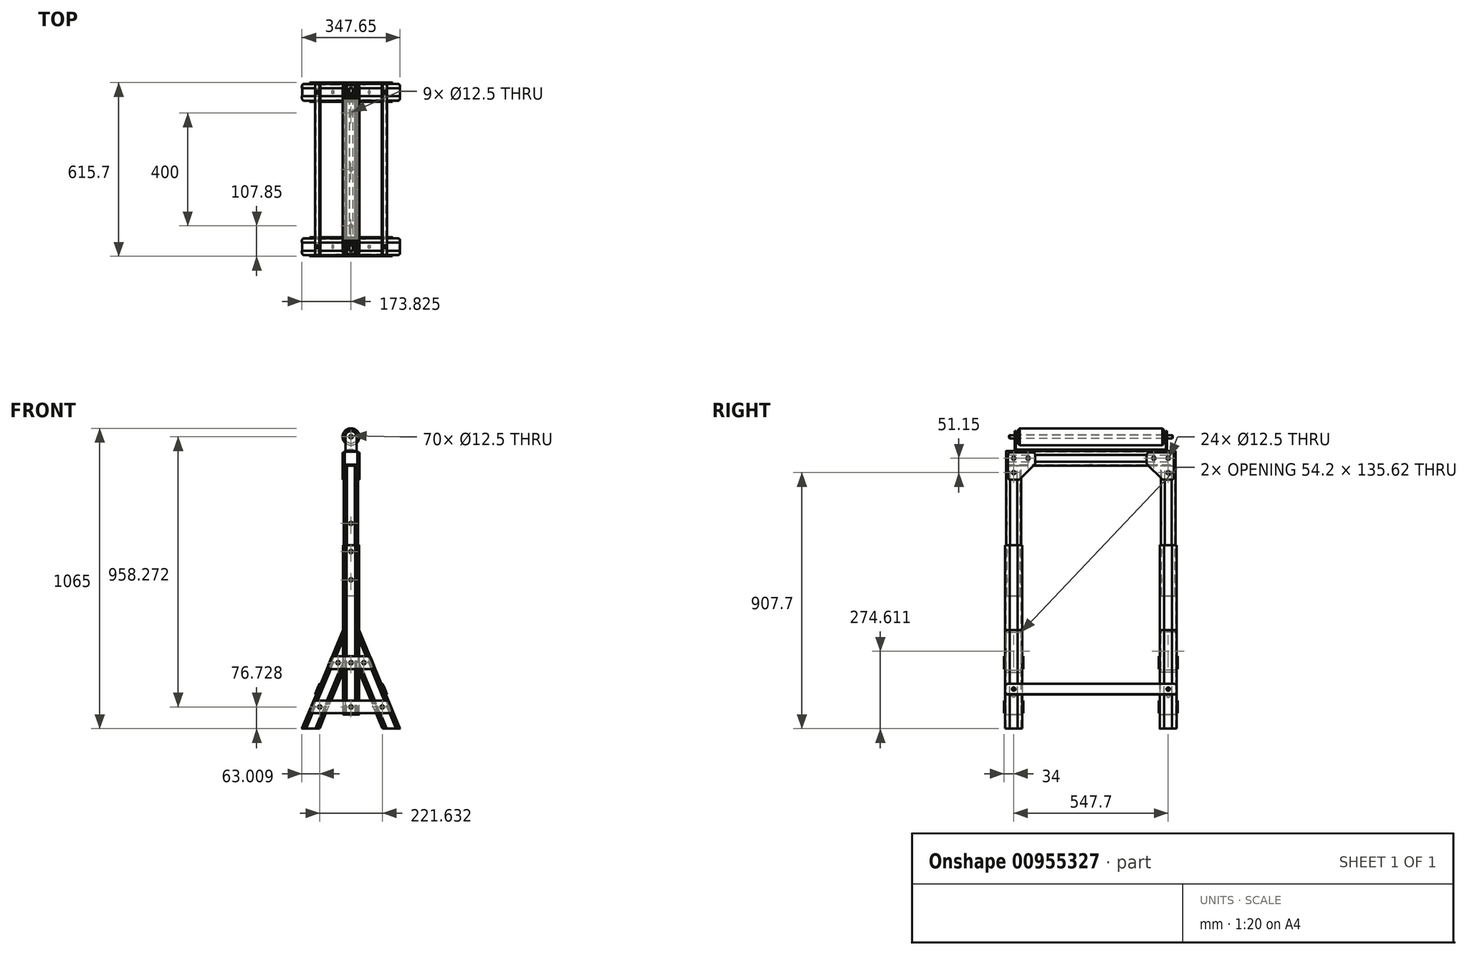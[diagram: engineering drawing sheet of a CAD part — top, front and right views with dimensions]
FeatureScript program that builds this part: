
annotation { "Feature Type Name" : "Feature", "Feature Type Description" : "" }
export const myFeature = defineFeature(function(context is Context, id is Id, definition is map)
    precondition{}
    {
        {
            var Q0;
            Q0=qCreatedBy(makeId("Front.planeOp"),FACE);
            var sketch = newSketch(context, id + "F0", { "sketchPlane" : qUnion([Q0])});
            skLineSegment(sketch, "E0", {"start": v(-144.97, 350) * mm, "end": v(0, 0) * mm});
            skLineSegment(sketch, "E1", {"start": v(0, 0) * mm, "end": v(-62.45, 0) * mm});
            skLineSegment(sketch, "E2", {"start": v(-62.45, 0) * mm, "end": v(-198.28, 327.92) * mm});
            skLineSegment(sketch, "E3", {"start": v(-198.28, 327.92) * mm, "end": v(-144.97, 350) * mm});
            skSolve(sketch);
        }
        {
            var Q0;
            Q0=makeQuery(id+"F0.imprint","IMPRINT",FACE,{"disambiguationData":[TD([[makeQuery(id+"F0.imprint","IMPRINT",EDGE,{"derivedFrom":sQuery(id+"F0.wireOp",EDGE,"E0")}),-1.0]])]});
            extrude(context, id + "F1", {"entities" : qUnion([Q0]), "depth" : 60 * mm, "offsetDistance" : 25 * mm});
        }
        {
            var Q0;
            Q0=makeQuery(id+"F1.opExtrude","CAP_EDGE",EDGE,{"disambiguationData":[OSD([sQuery(id+"F0.wireOp",EDGE,"E0")])],"isStart":false});
            var Q1;
            Q1=makeQuery(id+"F1.opExtrude","CAP_EDGE",EDGE,{"disambiguationData":[OSD([sQuery(id+"F0.wireOp",EDGE,"E0")])],"isStart":true});
            var Q2;
            Q2=makeQuery(id+"F1.opExtrude","CAP_EDGE",EDGE,{"disambiguationData":[OSD([sQuery(id+"F0.wireOp",EDGE,"E2")])],"isStart":true});
            var Q3;
            Q3=makeQuery(id+"F1.opExtrude","CAP_EDGE",EDGE,{"disambiguationData":[OSD([sQuery(id+"F0.wireOp",EDGE,"E2")])],"isStart":false});
            fillet(context, id + "F2", {"entities" : qUnion([Q0, Q1, Q2, Q3]), "radius" : 7.5 * mm, "tangentPropagation" : true, "allowEdgeOverflow" : false});
        }
        {
            var Q0;
            Q0=makeQuery(id+"F1.opExtrude","SWEPT_FACE",FACE,{"disambiguationData":[OSD([sQuery(id+"F0.wireOp",EDGE,"E3")])]});
            var sketch = newSketch(context, id + "F3", { "sketchPlane" : qUnion([Q0])});
            skArc(sketch, "E4.0", {"start": v(-50.2, -2.9) * mm, "mid": v(-53.45, -4.25) * mm, "end": v(-54.8, -7.5) * mm});
            skLineSegment(sketch, "E4.1", {"start": v(-54.8, -52.5) * mm, "end": v(-54.8, -7.5) * mm});
            skLineSegment(sketch, "E4.2", {"start": v(-50.2, -2.9) * mm, "end": v(-7.5, -2.9) * mm});
            skArc(sketch, "E4.3", {"start": v(-54.8, -52.5) * mm, "mid": v(-53.45, -55.75) * mm, "end": v(-50.2, -57.1) * mm});
            skArc(sketch, "E4.4", {"start": v(-2.9, -7.5) * mm, "mid": v(-4.25, -4.25) * mm, "end": v(-7.5, -2.9) * mm});
            skLineSegment(sketch, "E4.5", {"start": v(-2.9, -52.5) * mm, "end": v(-2.9, -7.5) * mm});
            skArc(sketch, "E4.6", {"start": v(-7.5, -57.1) * mm, "mid": v(-4.25, -55.75) * mm, "end": v(-2.9, -52.5) * mm});
            skLineSegment(sketch, "E4.7", {"start": v(-50.2, -57.1) * mm, "end": v(-7.5, -57.1) * mm});
            skLineSegment(sketch, "E5", {"start": v(-2.9, -7.5) * mm, "end": v(0, -7.5) * mm, "construction": true});
            skLineSegment(sketch, "E6", {"start": v(-2.9, -30) * mm, "end": v(0, -30) * mm, "construction": true});
            skLineSegment(sketch, "E7.0", {"start": v(-0.3, -44) * mm, "end": v(-0.3, -16) * mm});
            skLineSegment(sketch, "E8", {"start": v(-0.3, -16) * mm, "end": v(0, -16) * mm});
            skLineSegment(sketch, "E9", {"start": v(-0.3, -44) * mm, "end": v(0, -44) * mm});
            skLineSegment(sketch, "E10", {"start": v(-7.5, -57.1) * mm, "end": v(-7.5, -60) * mm, "construction": true});
            skLineSegment(sketch, "E11", {"start": v(-7.5, -60) * mm, "end": v(-8.5, -59) * mm});
            skLineSegment(sketch, "E12", {"start": v(-8.5, -59) * mm, "end": v(-9.5, -60) * mm});
            skLineSegment(sketch, "E13.1.0.0", {"start": v(-9.5, -60) * mm, "end": v(-10.5, -59) * mm});
            skLineSegment(sketch, "E13.1.0.1", {"start": v(-10.5, -59) * mm, "end": v(-11.5, -60) * mm});
            skLineSegment(sketch, "E13.2.0.0", {"start": v(-11.5, -60) * mm, "end": v(-12.5, -59) * mm});
            skLineSegment(sketch, "E13.2.0.1", {"start": v(-12.5, -59) * mm, "end": v(-13.5, -60) * mm});
            skLineSegment(sketch, "E13.direction1", {"start": v(-7.5, -60) * mm, "end": v(-9.5, -60) * mm, "construction": true});
            skLineSegment(sketch, "E14", {"start": v(-28.85, -60) * mm, "end": v(-28.85, -57.1) * mm, "construction": true});
            skLineSegment(sketch, "E15.MirrorCS", {"start": v(-50.2, -60) * mm, "end": v(-49.2, -59) * mm});
            skLineSegment(sketch, "E16.MirrorCS", {"start": v(-49.2, -59) * mm, "end": v(-48.2, -60) * mm});
            skLineSegment(sketch, "E17.MirrorCS", {"start": v(-48.2, -60) * mm, "end": v(-47.2, -59) * mm});
            skLineSegment(sketch, "E18.MirrorCS", {"start": v(-47.2, -59) * mm, "end": v(-46.2, -60) * mm});
            skLineSegment(sketch, "E19.MirrorCS", {"start": v(-46.2, -60) * mm, "end": v(-45.2, -59) * mm});
            skLineSegment(sketch, "E20.MirrorCS", {"start": v(-45.2, -59) * mm, "end": v(-44.2, -60) * mm});
            skLineSegment(sketch, "E21.MirrorCS", {"start": v(-57.4, -16) * mm, "end": v(-57.7, -16) * mm});
            skLineSegment(sketch, "E22.MirrorCS", {"start": v(-57.4, -44) * mm, "end": v(-57.4, -16) * mm});
            skLineSegment(sketch, "E23.MirrorCS", {"start": v(-57.4, -44) * mm, "end": v(-57.7, -44) * mm});
            skLineSegment(sketch, "E24.MirrorCS", {"start": v(-7.5, 0) * mm, "end": v(-8.5, -1) * mm});
            skLineSegment(sketch, "E25.MirrorCS", {"start": v(-8.5, -1) * mm, "end": v(-9.5, 0) * mm});
            skLineSegment(sketch, "E26.MirrorCS", {"start": v(-9.5, 0) * mm, "end": v(-10.5, -1) * mm});
            skLineSegment(sketch, "E27.MirrorCS", {"start": v(-10.5, -1) * mm, "end": v(-11.5, 0) * mm});
            skLineSegment(sketch, "E28.MirrorCS", {"start": v(-11.5, 0) * mm, "end": v(-12.5, -1) * mm});
            skLineSegment(sketch, "E29.MirrorCS", {"start": v(-12.5, -1) * mm, "end": v(-13.5, 0) * mm});
            skLineSegment(sketch, "E30.MirrorCS", {"start": v(-45.2, -1) * mm, "end": v(-44.2, 0) * mm});
            skLineSegment(sketch, "E31.MirrorCS", {"start": v(-46.2, 0) * mm, "end": v(-45.2, -1) * mm});
            skLineSegment(sketch, "E32.MirrorCS", {"start": v(-47.2, -1) * mm, "end": v(-46.2, 0) * mm});
            skLineSegment(sketch, "E33.MirrorCS", {"start": v(-48.2, 0) * mm, "end": v(-47.2, -1) * mm});
            skLineSegment(sketch, "E34.MirrorCS", {"start": v(-49.2, -1) * mm, "end": v(-48.2, 0) * mm});
            skLineSegment(sketch, "E35.MirrorCS", {"start": v(-50.2, 0) * mm, "end": v(-49.2, -1) * mm});
            skSolve(sketch);
        }
        {
            var Q0;
            {var subQ0=sQuery(id+"F3.wireOp",EDGE,"E24.MirrorCS");Q0=makeQuery(id+"F3.imprint","IMPRINT",FACE,{"disambiguationData":[TD([[makeQuery(id+"F3.imprint","IMPRINT",EDGE,{"derivedFrom":subQ0}),-1.0]])]});}
            var Q1;
            {var subQ0=sQuery(id+"F3.wireOp",EDGE,"E26.MirrorCS");Q1=makeQuery(id+"F3.imprint","IMPRINT",FACE,{"disambiguationData":[TD([[makeQuery(id+"F3.imprint","IMPRINT",EDGE,{"derivedFrom":subQ0}),-1.0]])]});}
            var Q2;
            {var subQ0=sQuery(id+"F3.wireOp",EDGE,"E28.MirrorCS");Q2=makeQuery(id+"F3.imprint","IMPRINT",FACE,{"disambiguationData":[TD([[makeQuery(id+"F3.imprint","IMPRINT",EDGE,{"derivedFrom":subQ0}),-1.0]])]});}
            var Q3;
            Q3=makeQuery(id+"F3.imprint","IMPRINT",FACE,{"disambiguationData":[TD([[makeQuery(id+"F3.imprint","IMPRINT",EDGE,{"derivedFrom":sQuery(id+"F3.wireOp",EDGE,"E4.0")}),1.0]])]});
            var Q4;
            {var subQ0=sQuery(id+"F3.wireOp",EDGE,"E30.MirrorCS");Q4=makeQuery(id+"F3.imprint","IMPRINT",FACE,{"disambiguationData":[TD([[makeQuery(id+"F3.imprint","IMPRINT",EDGE,{"derivedFrom":subQ0}),1.0]])]});}
            var Q5;
            {var subQ0=sQuery(id+"F3.wireOp",EDGE,"E32.MirrorCS");Q5=makeQuery(id+"F3.imprint","IMPRINT",FACE,{"disambiguationData":[TD([[makeQuery(id+"F3.imprint","IMPRINT",EDGE,{"derivedFrom":subQ0}),1.0]])]});}
            var Q6;
            {var subQ0=sQuery(id+"F3.wireOp",EDGE,"E34.MirrorCS");Q6=makeQuery(id+"F3.imprint","IMPRINT",FACE,{"disambiguationData":[TD([[makeQuery(id+"F3.imprint","IMPRINT",EDGE,{"derivedFrom":subQ0}),1.0]])]});}
            var Q7;
            {var subQ0=sQuery(id+"F3.wireOp",EDGE,"E21.MirrorCS");Q7=makeQuery(id+"F3.imprint","IMPRINT",FACE,{"disambiguationData":[TD([[makeQuery(id+"F3.imprint","IMPRINT",EDGE,{"derivedFrom":subQ0}),1.0]])]});}
            var Q8;
            {var subQ0=sQuery(id+"F3.wireOp",EDGE,"E15.MirrorCS");Q8=makeQuery(id+"F3.imprint","IMPRINT",FACE,{"disambiguationData":[TD([[makeQuery(id+"F3.imprint","IMPRINT",EDGE,{"derivedFrom":subQ0}),-1.0]])]});}
            var Q9;
            {var subQ0=sQuery(id+"F3.wireOp",EDGE,"E17.MirrorCS");Q9=makeQuery(id+"F3.imprint","IMPRINT",FACE,{"disambiguationData":[TD([[makeQuery(id+"F3.imprint","IMPRINT",EDGE,{"derivedFrom":subQ0}),-1.0]])]});}
            var Q10;
            {var subQ0=sQuery(id+"F3.wireOp",EDGE,"E19.MirrorCS");Q10=makeQuery(id+"F3.imprint","IMPRINT",FACE,{"disambiguationData":[TD([[makeQuery(id+"F3.imprint","IMPRINT",EDGE,{"derivedFrom":subQ0}),-1.0]])]});}
            var Q11;
            {var subQ0=sQuery(id+"F3.wireOp",EDGE,"E11");Q11=makeQuery(id+"F3.imprint","IMPRINT",FACE,{"disambiguationData":[TD([[makeQuery(id+"F3.imprint","IMPRINT",EDGE,{"derivedFrom":subQ0}),1.0]])]});}
            var Q12;
            {var subQ0=sQuery(id+"F3.wireOp",EDGE,"E13.1.0.0");Q12=makeQuery(id+"F3.imprint","IMPRINT",FACE,{"disambiguationData":[TD([[makeQuery(id+"F3.imprint","IMPRINT",EDGE,{"derivedFrom":subQ0}),1.0]])]});}
            var Q13;
            {var subQ0=sQuery(id+"F3.wireOp",EDGE,"E13.2.0.0");Q13=makeQuery(id+"F3.imprint","IMPRINT",FACE,{"disambiguationData":[TD([[makeQuery(id+"F3.imprint","IMPRINT",EDGE,{"derivedFrom":subQ0}),1.0]])]});}
            var Q14;
            Q14=makeQuery(id+"F3.imprint","IMPRINT",FACE,{"disambiguationData":[TD([[makeQuery(id+"F3.imprint","IMPRINT",EDGE,{"derivedFrom":sQuery(id+"F3.wireOp",EDGE,"E7.0")}),-1.0]])]});
            extrude(context, id + "F4", {"entities" : qUnion([Q0, Q1, Q2, Q3, Q4, Q5, Q6, Q7, Q8, Q9, Q10, Q11, Q12, Q13, Q14]), "operationType" : NewBodyOperationType.REMOVE, "endBound" : BoundingType.THROUGH_ALL, "oppositeDirection" : true, "depth" : 25 * mm, "offsetDistance" : 25 * mm});
        }
        {
            var Q0;
            Q0=makeQuery(id+"F4.boolean.opBoolean","COPY",FACE,{"derivedFrom":makeQuery(id+"F4.opExtrude","SWEPT_FACE",FACE,{"disambiguationData":[OSD([sQuery(id+"F3.wireOp",EDGE,"E7.0")])]})});
            var sketch = newSketch(context, id + "F5", { "sketchPlane" : qUnion([Q0])});
            skCircle(sketch, "E36", {"center": v(-30, 150.12) * mm, "radius": 6.25 * mm});
            skSolve(sketch);
        }
        {
            var Q0;
            Q0 = qSketchRegion(id + "F5", true);
            var Q1;
            Q1=makeQuery(id+"F4.boolean.opBoolean","COPY",FACE,{"derivedFrom":makeQuery(id+"F4.opExtrude","SWEPT_FACE",FACE,{"disambiguationData":[OSD([sQuery(id+"F3.wireOp",EDGE,"E22.MirrorCS")])]})});
            extrude(context, id + "F6", {"entities" : qUnion([Q0]), "operationType" : NewBodyOperationType.REMOVE, "endBound" : BoundingType.UP_TO_SURFACE, "oppositeDirection" : true, "depth" : 25 * mm, "endBoundEntityFace" : qUnion([Q1]), "offsetDistance" : 25 * mm});
        }
        {
            var Q0;
            Q0=makeQuery(id+"F1.opExtrude","CAP_FACE",FACE,{"disambiguationData":[OSD([sQuery(id+"F0.wireOp",EDGE,"E0"),sQuery(id+"F0.wireOp",EDGE,"E1"),sQuery(id+"F0.wireOp",EDGE,"E2"),sQuery(id+"F0.wireOp",EDGE,"E3")])],"isStart":false});
            var sketch = newSketch(context, id + "F7", { "sketchPlane" : qUnion([Q0])});
            skLineSegment(sketch, "E37", {"start": v(-198.28, 327.92) * mm, "end": v(-144.97, 350) * mm});
            skLineSegment(sketch, "E38", {"start": v(-144.97, 350) * mm, "end": v(-144.97, 199.22) * mm});
            skLineSegment(sketch, "E39", {"start": v(-144.97, 199.22) * mm, "end": v(-198.28, 327.92) * mm});
            skSolve(sketch);
        }
        {
            var Q0;
            Q0=qSketchRegion(id+"F7",true);
            var Q1;
            Q1=makeQuery(id+"F1.opExtrude","CAP_FACE",FACE,{"disambiguationData":[OSD([sQuery(id+"F0.wireOp",EDGE,"E0"),sQuery(id+"F0.wireOp",EDGE,"E1"),sQuery(id+"F0.wireOp",EDGE,"E2"),sQuery(id+"F0.wireOp",EDGE,"E3")])],"isStart":true});
            extrude(context, id + "F8", {"entities" : qUnion([Q0]), "operationType" : NewBodyOperationType.REMOVE, "endBound" : BoundingType.UP_TO_SURFACE, "oppositeDirection" : true, "depth" : 25 * mm, "endBoundEntityFace" : qUnion([Q1]), "offsetDistance" : 25 * mm});
        }
        {
            var Q0;
            Q0=makeQuery(id+"F1.opExtrude","CAP_FACE",FACE,{"disambiguationData":[OSD([sQuery(id+"F0.wireOp",EDGE,"E0"),sQuery(id+"F0.wireOp",EDGE,"E1"),sQuery(id+"F0.wireOp",EDGE,"E2"),sQuery(id+"F0.wireOp",EDGE,"E3")])],"isStart":false});
            var sketch = newSketch(context, id + "F9", { "sketchPlane" : qUnion([Q0])});
            skLineSegment(sketch, "E40", {"start": v(-202.67, 650) * mm, "end": v(-202.67, 50) * mm});
            skLineSegment(sketch, "E41", {"start": v(-202.67, 50) * mm, "end": v(-144.97, 50) * mm});
            skLineSegment(sketch, "E42", {"start": v(-144.97, 50) * mm, "end": v(-144.97, 650) * mm});
            skLineSegment(sketch, "E43", {"start": v(-144.97, 650) * mm, "end": v(-202.67, 650) * mm});
            skSolve(sketch);
        }
        {
            var Q0;
            Q0 = qSketchRegion(id + "F9", true);
            extrude(context, id + "F10", {"entities" : qUnion([Q0]), "oppositeDirection" : true, "depth" : 60 * mm, "offsetDistance" : 25 * mm});
        }
        {
            var Q0;
            {var subQ0=sQuery(id+"F0.wireOp",EDGE,"E0");var subQ1=sQuery(id+"F0.wireOp",EDGE,"E3");Q0=makeQuery(id+"F8.boolean.opBoolean","MERGE",EDGE,{"derivedFrom":[makeQuery(id+"F4.boolean.opBoolean","SPLIT",EDGE,{"disambiguationData":[TD([makeQuery(id+"F4.opExtrude","SWEPT_FACE",FACE,{"disambiguationData":[OSD([sQuery(id+"F3.wireOp",EDGE,"E9")])]})])],"derivedFrom":makeQuery(id+"F1.opExtrude","SWEPT_EDGE",EDGE,{"disambiguationData":[OSD([subQ0,subQ1])]})})],"fromTools":[makeQuery(id+"F8.opExtrude","SWEPT_EDGE",EDGE,{"disambiguationData":[OSD([sQuery(id+"F7.wireOp",EDGE,"E37"),sQuery(id+"F7.wireOp",EDGE,"E38")])]})]});}
            cPlane(context, id + "F11", {"entities" : qUnion([Q0]), "cplaneType" : CPlaneType.LINE_ANGLE, "offset" : 25 * mm, "angle" : 0 * degree, "width" : 150 * mm, "height" : 150 * mm});
        }
        {
            var Q0;
            Q0=makeQuery(id+"F10.opExtrude","CAP_EDGE",EDGE,{"disambiguationData":[OSD([sQuery(id+"F9.wireOp",EDGE,"E40")])],"isStart":true});
            var Q1;
            Q1=makeQuery(id+"F10.opExtrude","CAP_EDGE",EDGE,{"disambiguationData":[OSD([sQuery(id+"F9.wireOp",EDGE,"E42")])],"isStart":true});
            var Q2;
            Q2=makeQuery(id+"F10.opExtrude","CAP_EDGE",EDGE,{"disambiguationData":[OSD([sQuery(id+"F9.wireOp",EDGE,"E40")])],"isStart":false});
            var Q3;
            Q3=makeQuery(id+"F10.opExtrude","CAP_EDGE",EDGE,{"disambiguationData":[OSD([sQuery(id+"F9.wireOp",EDGE,"E42")])],"isStart":false});
            fillet(context, id + "F12", {"entities" : qUnion([Q0, Q1, Q2, Q3]), "radius" : 7.5 * mm, "tangentPropagation" : true, "allowEdgeOverflow" : false});
        }
        {
            var Q0;
            Q0=makeQuery(id+"F10.opExtrude","SWEPT_FACE",FACE,{"disambiguationData":[OSD([sQuery(id+"F9.wireOp",EDGE,"E43")])]});
            var sketch = newSketch(context, id + "F13", { "sketchPlane" : qUnion([Q0])});
            skLineSegment(sketch, "E44", {"start": v(-202.67, -30) * mm, "end": v(-144.97, -30) * mm, "construction": true});
            skLineSegment(sketch, "E45.2", {"start": v(-199.77, -30) * mm, "end": v(-199.77, -52.5) * mm});
            skArc(sketch, "E45.4", {"start": v(-199.77, -52.5) * mm, "mid": v(-198.43, -55.75) * mm, "end": v(-195.17, -57.1) * mm});
            skLineSegment(sketch, "E45.5", {"start": v(-195.17, -57.1) * mm, "end": v(-152.47, -57.1) * mm});
            skArc(sketch, "E45.6", {"start": v(-152.47, -57.1) * mm, "mid": v(-149.22, -55.75) * mm, "end": v(-147.87, -52.5) * mm});
            skLineSegment(sketch, "E45.7", {"start": v(-147.87, -52.5) * mm, "end": v(-147.87, -30) * mm});
            skLineSegment(sketch, "E46", {"start": v(-145.27, -30) * mm, "end": v(-145.27, -44) * mm});
            skLineSegment(sketch, "E47", {"start": v(-145.27, -44) * mm, "end": v(-144.97, -44) * mm});
            skLineSegment(sketch, "E48", {"start": v(-202.37, -30) * mm, "end": v(-202.37, -44) * mm});
            skLineSegment(sketch, "E49", {"start": v(-202.37, -44) * mm, "end": v(-202.67, -44) * mm});
            skLineSegment(sketch, "E50", {"start": v(-195.17, -60) * mm, "end": v(-194.17, -59) * mm});
            skLineSegment(sketch, "E51", {"start": v(-194.17, -59) * mm, "end": v(-193.17, -60) * mm});
            skLineSegment(sketch, "E52.1.0.0", {"start": v(-193.17, -60) * mm, "end": v(-192.17, -59) * mm});
            skLineSegment(sketch, "E52.1.0.1", {"start": v(-192.17, -59) * mm, "end": v(-191.17, -60) * mm});
            skLineSegment(sketch, "E52.2.0.0", {"start": v(-191.17, -60) * mm, "end": v(-190.17, -59) * mm});
            skLineSegment(sketch, "E52.2.0.1", {"start": v(-190.17, -59) * mm, "end": v(-189.17, -60) * mm});
            skLineSegment(sketch, "E52.direction1", {"start": v(-195.17, -60) * mm, "end": v(-193.17, -60) * mm, "construction": true});
            skLineSegment(sketch, "E53", {"start": v(-152.47, -60) * mm, "end": v(-153.47, -59) * mm});
            skLineSegment(sketch, "E54", {"start": v(-153.47, -59) * mm, "end": v(-154.47, -60) * mm});
            skLineSegment(sketch, "E55.1.0.0", {"start": v(-154.47, -60) * mm, "end": v(-155.47, -59) * mm});
            skLineSegment(sketch, "E55.1.0.1", {"start": v(-155.47, -59) * mm, "end": v(-156.47, -60) * mm});
            skLineSegment(sketch, "E55.2.0.0", {"start": v(-156.47, -60) * mm, "end": v(-157.47, -59) * mm});
            skLineSegment(sketch, "E55.2.0.1", {"start": v(-157.47, -59) * mm, "end": v(-158.47, -60) * mm});
            skLineSegment(sketch, "E55.direction1", {"start": v(-152.47, -60) * mm, "end": v(-154.47, -60) * mm, "construction": true});
            skLineSegment(sketch, "E56.MirrorCS", {"start": v(-153.47, -1) * mm, "end": v(-154.47, 0) * mm});
            skLineSegment(sketch, "E57.MirrorCS", {"start": v(-152.47, 0) * mm, "end": v(-154.47, 0) * mm, "construction": true});
            skLineSegment(sketch, "E58.MirrorCS", {"start": v(-154.47, 0) * mm, "end": v(-155.47, -1) * mm});
            skLineSegment(sketch, "E59.MirrorCS", {"start": v(-152.47, 0) * mm, "end": v(-153.47, -1) * mm});
            skLineSegment(sketch, "E60.MirrorCS", {"start": v(-155.47, -1) * mm, "end": v(-156.47, 0) * mm});
            skLineSegment(sketch, "E61.MirrorCS", {"start": v(-193.17, 0) * mm, "end": v(-192.17, -1) * mm});
            skLineSegment(sketch, "E62.MirrorCS", {"start": v(-195.17, 0) * mm, "end": v(-193.17, 0) * mm, "construction": true});
            skLineSegment(sketch, "E63.MirrorCS", {"start": v(-194.17, -1) * mm, "end": v(-193.17, 0) * mm});
            skLineSegment(sketch, "E64.MirrorCS", {"start": v(-192.17, -1) * mm, "end": v(-191.17, 0) * mm});
            skLineSegment(sketch, "E65.MirrorCS", {"start": v(-191.17, 0) * mm, "end": v(-190.17, -1) * mm});
            skLineSegment(sketch, "E66.MirrorCS", {"start": v(-195.17, 0) * mm, "end": v(-194.17, -1) * mm});
            skLineSegment(sketch, "E67.MirrorCS", {"start": v(-190.17, -1) * mm, "end": v(-189.17, 0) * mm});
            skLineSegment(sketch, "E68.MirrorCS", {"start": v(-156.47, 0) * mm, "end": v(-157.47, -1) * mm});
            skLineSegment(sketch, "E69.MirrorCS", {"start": v(-202.37, -16) * mm, "end": v(-202.67, -16) * mm});
            skLineSegment(sketch, "E70.MirrorCS", {"start": v(-157.47, -1) * mm, "end": v(-158.47, 0) * mm});
            skLineSegment(sketch, "E71.MirrorCS", {"start": v(-145.27, -16) * mm, "end": v(-144.97, -16) * mm});
            skLineSegment(sketch, "E72.MirrorCS", {"start": v(-147.87, -7.5) * mm, "end": v(-147.87, -30) * mm});
            skLineSegment(sketch, "E73.MirrorCS", {"start": v(-199.77, -30) * mm, "end": v(-199.77, -7.5) * mm});
            skLineSegment(sketch, "E74.MirrorCS", {"start": v(-195.17, -2.9) * mm, "end": v(-152.47, -2.9) * mm});
            skLineSegment(sketch, "E75.MirrorCS", {"start": v(-145.27, -30) * mm, "end": v(-145.27, -16) * mm});
            skLineSegment(sketch, "E76.MirrorCS", {"start": v(-202.37, -30) * mm, "end": v(-202.37, -16) * mm});
            skArc(sketch, "E77.MirrorCS", {"start": v(-199.77, -7.5) * mm, "mid": v(-198.43, -4.25) * mm, "end": v(-195.17, -2.9) * mm});
            skArc(sketch, "E78.MirrorCS", {"start": v(-152.47, -2.9) * mm, "mid": v(-149.22, -4.25) * mm, "end": v(-147.87, -7.5) * mm});
            skSolve(sketch);
        }
        {
            var Q0;
            {var subQ0=sQuery(id+"F13.wireOp",EDGE,"E63.MirrorCS");Q0=makeQuery(id+"F13.imprint","IMPRINT",FACE,{"disambiguationData":[TD([[makeQuery(id+"F13.imprint","IMPRINT",EDGE,{"derivedFrom":subQ0}),1.0]])]});}
            var Q1;
            {var subQ0=sQuery(id+"F13.wireOp",EDGE,"E61.MirrorCS");Q1=makeQuery(id+"F13.imprint","IMPRINT",FACE,{"disambiguationData":[TD([[makeQuery(id+"F13.imprint","IMPRINT",EDGE,{"derivedFrom":subQ0}),1.0]])]});}
            var Q2;
            {var subQ0=sQuery(id+"F13.wireOp",EDGE,"E65.MirrorCS");Q2=makeQuery(id+"F13.imprint","IMPRINT",FACE,{"disambiguationData":[TD([[makeQuery(id+"F13.imprint","IMPRINT",EDGE,{"derivedFrom":subQ0}),1.0]])]});}
            var Q3;
            Q3=makeQuery(id+"F13.imprint","IMPRINT",FACE,{"disambiguationData":[TD([[makeQuery(id+"F13.imprint","IMPRINT",EDGE,{"derivedFrom":sQuery(id+"F13.wireOp",EDGE,"E45.2")}),1.0]])]});
            var Q4;
            {var subQ0=sQuery(id+"F13.wireOp",EDGE,"E56.MirrorCS");Q4=makeQuery(id+"F13.imprint","IMPRINT",FACE,{"disambiguationData":[TD([[makeQuery(id+"F13.imprint","IMPRINT",EDGE,{"derivedFrom":subQ0}),-1.0]])]});}
            var Q5;
            {var subQ0=sQuery(id+"F13.wireOp",EDGE,"E58.MirrorCS");Q5=makeQuery(id+"F13.imprint","IMPRINT",FACE,{"disambiguationData":[TD([[makeQuery(id+"F13.imprint","IMPRINT",EDGE,{"derivedFrom":subQ0}),-1.0]])]});}
            var Q6;
            {var subQ0=sQuery(id+"F13.wireOp",EDGE,"E68.MirrorCS");Q6=makeQuery(id+"F13.imprint","IMPRINT",FACE,{"disambiguationData":[TD([[makeQuery(id+"F13.imprint","IMPRINT",EDGE,{"derivedFrom":subQ0}),-1.0]])]});}
            var Q7;
            {var subQ0=sQuery(id+"F13.wireOp",EDGE,"E50");Q7=makeQuery(id+"F13.imprint","IMPRINT",FACE,{"disambiguationData":[TD([[makeQuery(id+"F13.imprint","IMPRINT",EDGE,{"derivedFrom":subQ0}),-1.0]])]});}
            var Q8;
            {var subQ0=sQuery(id+"F13.wireOp",EDGE,"E52.1.0.0");Q8=makeQuery(id+"F13.imprint","IMPRINT",FACE,{"disambiguationData":[TD([[makeQuery(id+"F13.imprint","IMPRINT",EDGE,{"derivedFrom":subQ0}),-1.0]])]});}
            var Q9;
            {var subQ0=sQuery(id+"F13.wireOp",EDGE,"E52.2.0.0");Q9=makeQuery(id+"F13.imprint","IMPRINT",FACE,{"disambiguationData":[TD([[makeQuery(id+"F13.imprint","IMPRINT",EDGE,{"derivedFrom":subQ0}),-1.0]])]});}
            var Q10;
            {var subQ0=sQuery(id+"F13.wireOp",EDGE,"E53");Q10=makeQuery(id+"F13.imprint","IMPRINT",FACE,{"disambiguationData":[TD([[makeQuery(id+"F13.imprint","IMPRINT",EDGE,{"derivedFrom":subQ0}),1.0]])]});}
            var Q11;
            {var subQ0=sQuery(id+"F13.wireOp",EDGE,"E55.1.0.0");Q11=makeQuery(id+"F13.imprint","IMPRINT",FACE,{"disambiguationData":[TD([[makeQuery(id+"F13.imprint","IMPRINT",EDGE,{"derivedFrom":subQ0}),1.0]])]});}
            var Q12;
            {var subQ0=sQuery(id+"F13.wireOp",EDGE,"E55.2.0.0");Q12=makeQuery(id+"F13.imprint","IMPRINT",FACE,{"disambiguationData":[TD([[makeQuery(id+"F13.imprint","IMPRINT",EDGE,{"derivedFrom":subQ0}),1.0]])]});}
            var Q13;
            Q13=makeQuery(id+"F13.imprint","IMPRINT",FACE,{"disambiguationData":[TD([[makeQuery(id+"F13.imprint","IMPRINT",EDGE,{"derivedFrom":sQuery(id+"F13.wireOp",EDGE,"E48")}),-1.0]])]});
            var Q14;
            Q14=makeQuery(id+"F13.imprint","IMPRINT",FACE,{"disambiguationData":[TD([[makeQuery(id+"F13.imprint","IMPRINT",EDGE,{"derivedFrom":sQuery(id+"F13.wireOp",EDGE,"E46")}),1.0]])]});
            var Q15;
            Q15=makeQuery(id+"F10.opExtrude","SWEPT_FACE",FACE,{"disambiguationData":[OSD([sQuery(id+"F9.wireOp",EDGE,"E41")])]});
            extrude(context, id + "F14", {"entities" : qUnion([Q0, Q1, Q2, Q3, Q4, Q5, Q6, Q7, Q8, Q9, Q10, Q11, Q12, Q13, Q14]), "operationType" : NewBodyOperationType.REMOVE, "endBound" : BoundingType.UP_TO_SURFACE, "oppositeDirection" : true, "depth" : 25 * mm, "endBoundEntityFace" : qUnion([Q15]), "offsetDistance" : 25 * mm});
        }
        {
            var Q0;
            Q0=makeQuery(id+"F1.opExtrude","CAP_FACE",FACE,{"disambiguationData":[OSD([sQuery(id+"F0.wireOp",EDGE,"E0"),sQuery(id+"F0.wireOp",EDGE,"E1"),sQuery(id+"F0.wireOp",EDGE,"E2"),sQuery(id+"F0.wireOp",EDGE,"E3")])],"isStart":false});
            var sketch = newSketch(context, id + "F15", { "sketchPlane" : qUnion([Q0])});
            skCircle(sketch, "E79", {"center": v(-128.07, 233.79) * mm, "radius": 6.25 * mm});
            skLineSegment(sketch, "E80", {"start": v(-144.97, 274.61) * mm, "end": v(-31.23, 0) * mm, "construction": true});
            skCircle(sketch, "E81", {"center": v(-63, 76.73) * mm, "radius": 6.25 * mm});
            skLineSegment(sketch, "E82", {"start": v(0, 0) * mm, "end": v(63.08, 26.13) * mm, "construction": true});
            skSolve(sketch);
        }
        {
            var Q0;
            Q0 = qSketchRegion(id + "F15", true);
            var Q1;
            Q1=makeQuery(id+"F1.opExtrude","CAP_FACE",FACE,{"disambiguationData":[OSD([sQuery(id+"F0.wireOp",EDGE,"E0"),sQuery(id+"F0.wireOp",EDGE,"E1"),sQuery(id+"F0.wireOp",EDGE,"E2"),sQuery(id+"F0.wireOp",EDGE,"E3")])],"isStart":true});
            extrude(context, id + "F16", {"entities" : qUnion([Q0]), "operationType" : NewBodyOperationType.REMOVE, "endBound" : BoundingType.UP_TO_SURFACE, "oppositeDirection" : true, "depth" : 25 * mm, "endBoundEntityFace" : qUnion([Q1]), "offsetDistance" : 25 * mm});
        }
        {
            var Q0;
            Q0=makeQuery(id+"F14.boolean.opBoolean","COPY",FACE,{"derivedFrom":makeQuery(id+"F14.opExtrude","SWEPT_FACE",FACE,{"disambiguationData":[OSD([sQuery(id+"F13.wireOp",EDGE,"E48"),sQuery(id+"F13.wireOp",EDGE,"E76.MirrorCS")])]})});
            var Q1;
            Q1=makeQuery(id+"F14.boolean.opBoolean","COPY",FACE,{"derivedFrom":makeQuery(id+"F14.opExtrude","SWEPT_FACE",FACE,{"disambiguationData":[OSD([sQuery(id+"F13.wireOp",EDGE,"E46"),sQuery(id+"F13.wireOp",EDGE,"E75.MirrorCS")])]})});
            cPlane(context, id + "F17", {"entities" : qUnion([Q0, Q1]), "cplaneType" : CPlaneType.MID_PLANE, "offset" : 25 * mm, "width" : 150 * mm, "height" : 150 * mm});
        }
        {
            var Q0;
            Q0=makeQuery(id+"F1.opExtrude","SWEPT_BODY",BODY,{"disambiguationData":[OSD([sQuery(id+"F0.wireOp",EDGE,"E0"),sQuery(id+"F0.wireOp",EDGE,"E1"),sQuery(id+"F0.wireOp",EDGE,"E2"),sQuery(id+"F0.wireOp",EDGE,"E3")])]});
            var Q1;
            Q1=qCreatedBy(id+"F17.planeOp",FACE);
            mirror(context, id + "F18", {"entities" : qUnion([Q0]), "mirrorPlane" : qUnion([Q1])});
        }
        {
            var Q0;
            Q0=makeQuery(id+"F1.opExtrude","CAP_FACE",FACE,{"disambiguationData":[OSD([sQuery(id+"F0.wireOp",EDGE,"E0"),sQuery(id+"F0.wireOp",EDGE,"E1"),sQuery(id+"F0.wireOp",EDGE,"E2"),sQuery(id+"F0.wireOp",EDGE,"E3")])],"isStart":false});
            var sketch = newSketch(context, id + "F19", { "sketchPlane" : qUnion([Q0])});
            skLineSegment(sketch, "E83", {"start": v(-241.5, 256.29) * mm, "end": v(-106.16, 256.29) * mm});
            skLineSegment(sketch, "E84", {"start": v(-106.16, 256.29) * mm, "end": v(-87.52, 211.29) * mm});
            skLineSegment(sketch, "E85", {"start": v(-22.46, 54.23) * mm, "end": v(-325.19, 54.23) * mm});
            skLineSegment(sketch, "E86", {"start": v(-325.19, 54.23) * mm, "end": v(-306.55, 99.23) * mm});
            skCircle(sketch, "E87", {"center": v(-128.07, 233.79) * mm, "radius": 6.25 * mm});
            skCircle(sketch, "E88", {"center": v(-219.58, 233.79) * mm, "radius": 6.25 * mm});
            skCircle(sketch, "E89", {"center": v(-284.64, 76.73) * mm, "radius": 6.25 * mm});
            skCircle(sketch, "E90", {"center": v(-63, 76.73) * mm, "radius": 6.25 * mm});
            skLineSegment(sketch, "E91", {"start": v(-284.64, 76.73) * mm, "end": v(-63, 76.73) * mm, "construction": true});
            skLineSegment(sketch, "E92", {"start": v(-219.58, 233.79) * mm, "end": v(-128.07, 233.79) * mm, "construction": true});
            skLineSegment(sketch, "E93", {"start": v(-173.82, 233.79) * mm, "end": v(-173.82, 76.73) * mm, "construction": true});
            skCircle(sketch, "E94", {"center": v(-173.82, 233.79) * mm, "radius": 6.25 * mm});
            skCircle(sketch, "E95", {"center": v(-173.82, 76.73) * mm, "radius": 6.25 * mm});
            skLineSegment(sketch, "E96", {"start": v(-128.07, 233.79) * mm, "end": v(-128.07, 256.29) * mm, "construction": true});
            skLineSegment(sketch, "E97", {"start": v(-284.64, 76.73) * mm, "end": v(-284.64, 54.23) * mm, "construction": true});
            skLineSegment(sketch, "E98", {"start": v(-260.13, 211.29) * mm, "end": v(-87.52, 211.29) * mm});
            skLineSegment(sketch, "E99", {"start": v(-41.1, 99.23) * mm, "end": v(-306.55, 99.23) * mm});
            skLineSegment(sketch, "E100.trimOffspring", {"start": v(-260.13, 211.29) * mm, "end": v(-241.5, 256.29) * mm});
            skLineSegment(sketch, "E101.trimOffspring", {"start": v(-41.1, 99.23) * mm, "end": v(-22.46, 54.23) * mm});
            skLineSegment(sketch, "E102", {"start": v(-63, 76.73) * mm, "end": v(-63, 99.23) * mm, "construction": true});
            skLineSegment(sketch, "E103", {"start": v(-219.58, 233.79) * mm, "end": v(-219.58, 211.29) * mm, "construction": true});
            skSolve(sketch);
        }
        {
            var Q0;
            Q0 = qSketchRegion(id + "F19", true);
            extrude(context, id + "F20", {"entities" : qUnion([Q0]), "depth" : 4 * mm, "offsetDistance" : 25 * mm});
        }
        {
            var Q0;
            Q0=makeQuery(id+"F20.opExtrude","SWEPT_EDGE",EDGE,{"disambiguationData":[OSD([sQuery(id+"F19.wireOp",EDGE,"E85"),sQuery(id+"F19.wireOp",EDGE,"E101.trimOffspring")])]});
            var Q1;
            Q1=makeQuery(id+"F20.opExtrude","SWEPT_EDGE",EDGE,{"disambiguationData":[OSD([sQuery(id+"F19.wireOp",EDGE,"E85"),sQuery(id+"F19.wireOp",EDGE,"E86")])]});
            var Q2;
            Q2=makeQuery(id+"F20.opExtrude","SWEPT_EDGE",EDGE,{"disambiguationData":[OSD([sQuery(id+"F19.wireOp",EDGE,"E86"),sQuery(id+"F19.wireOp",EDGE,"E99")])]});
            var Q3;
            Q3=makeQuery(id+"F20.opExtrude","SWEPT_EDGE",EDGE,{"disambiguationData":[OSD([sQuery(id+"F19.wireOp",EDGE,"E83"),sQuery(id+"F19.wireOp",EDGE,"E100.trimOffspring")])]});
            var Q4;
            Q4=makeQuery(id+"F20.opExtrude","SWEPT_EDGE",EDGE,{"disambiguationData":[OSD([sQuery(id+"F19.wireOp",EDGE,"E98"),sQuery(id+"F19.wireOp",EDGE,"E100.trimOffspring")])]});
            var Q5;
            Q5=makeQuery(id+"F20.opExtrude","SWEPT_EDGE",EDGE,{"disambiguationData":[OSD([sQuery(id+"F19.wireOp",EDGE,"E84"),sQuery(id+"F19.wireOp",EDGE,"E98")])]});
            var Q6;
            Q6=makeQuery(id+"F20.opExtrude","SWEPT_EDGE",EDGE,{"disambiguationData":[OSD([sQuery(id+"F19.wireOp",EDGE,"E83"),sQuery(id+"F19.wireOp",EDGE,"E84")])]});
            var Q7;
            Q7=makeQuery(id+"F20.opExtrude","SWEPT_EDGE",EDGE,{"disambiguationData":[OSD([sQuery(id+"F19.wireOp",EDGE,"E99"),sQuery(id+"F19.wireOp",EDGE,"E101.trimOffspring")])]});
            fillet(context, id + "F21", {"entities" : qUnion([Q0, Q1, Q2, Q3, Q4, Q5, Q6, Q7]), "radius" : 10 * mm, "tangentPropagation" : true, "allowEdgeOverflow" : false});
        }
        {
            var Q0;
            Q0=makeQuery(id+"F10.opExtrude","CAP_FACE",FACE,{"disambiguationData":[OSD([sQuery(id+"F9.wireOp",EDGE,"E40"),sQuery(id+"F9.wireOp",EDGE,"E41"),sQuery(id+"F9.wireOp",EDGE,"E42"),sQuery(id+"F9.wireOp",EDGE,"E43")])],"isStart":true});
            var sketch = newSketch(context, id + "F22", { "sketchPlane" : qUnion([Q0])});
            skCircle(sketch, "E104", {"center": v(-173.82, 233.79) * mm, "radius": 6.25 * mm});
            skCircle(sketch, "E105", {"center": v(-173.82, 76.73) * mm, "radius": 6.25 * mm});
            skLineSegment(sketch, "E106", {"start": v(-276.86, 240.04) * mm, "end": v(0, 240.04) * mm, "construction": true});
            skSolve(sketch);
        }
        {
            var Q0;
            Q0 = qSketchRegion(id + "F22", true);
            var Q1;
            Q1=makeQuery(id+"F10.opExtrude","CAP_FACE",FACE,{"disambiguationData":[OSD([sQuery(id+"F9.wireOp",EDGE,"E40"),sQuery(id+"F9.wireOp",EDGE,"E41"),sQuery(id+"F9.wireOp",EDGE,"E42"),sQuery(id+"F9.wireOp",EDGE,"E43")])],"isStart":false});
            extrude(context, id + "F23", {"entities" : qUnion([Q0]), "operationType" : NewBodyOperationType.REMOVE, "endBound" : BoundingType.UP_TO_SURFACE, "oppositeDirection" : true, "depth" : 25 * mm, "endBoundEntityFace" : qUnion([Q1]), "offsetDistance" : 25 * mm});
        }
        {
            var Q0;
            Q0=makeQuery(id+"F18.opPattern","COPY",FACE,{"derivedFrom":makeQuery(id+"F1.opExtrude","CAP_FACE",FACE,{"disambiguationData":[OSD([sQuery(id+"F0.wireOp",EDGE,"E0"),sQuery(id+"F0.wireOp",EDGE,"E1"),sQuery(id+"F0.wireOp",EDGE,"E2"),sQuery(id+"F0.wireOp",EDGE,"E3")])],"isStart":true}),"instanceName":"1"});
            var Q1;
            Q1=makeQuery(id+"F18.opPattern","COPY",FACE,{"derivedFrom":makeQuery(id+"F1.opExtrude","CAP_FACE",FACE,{"disambiguationData":[OSD([sQuery(id+"F0.wireOp",EDGE,"E0"),sQuery(id+"F0.wireOp",EDGE,"E1"),sQuery(id+"F0.wireOp",EDGE,"E2"),sQuery(id+"F0.wireOp",EDGE,"E3")])],"isStart":false}),"instanceName":"1"});
            cPlane(context, id + "F24", {"entities" : qUnion([Q0, Q1]), "cplaneType" : CPlaneType.MID_PLANE, "offset" : 25 * mm, "width" : 150 * mm, "height" : 150 * mm});
        }
        {
            var Q0;
            Q0=makeQuery(id+"F20.opExtrude","SWEPT_BODY",BODY,{"disambiguationData":[OSD([sQuery(id+"F19.wireOp",EDGE,"E83"),sQuery(id+"F19.wireOp",EDGE,"E84"),sQuery(id+"F19.wireOp",EDGE,"E85"),sQuery(id+"F19.wireOp",EDGE,"E86"),sQuery(id+"F19.wireOp",EDGE,"E87"),sQuery(id+"F19.wireOp",EDGE,"E88"),sQuery(id+"F19.wireOp",EDGE,"E89"),sQuery(id+"F19.wireOp",EDGE,"E90"),sQuery(id+"F19.wireOp",EDGE,"E94"),sQuery(id+"F19.wireOp",EDGE,"E95")])]});
            var Q1;
            Q1=qCreatedBy(id+"F24.planeOp",FACE);
            mirror(context, id + "F25", {"entities" : qUnion([Q0]), "mirrorPlane" : qUnion([Q1])});
        }
        {
            var Q0;
            Q0=makeQuery(id+"F18.opPattern","COPY",FACE,{"derivedFrom":makeQuery(id+"F1.opExtrude","SWEPT_FACE",FACE,{"disambiguationData":[OSD([sQuery(id+"F0.wireOp",EDGE,"E1")])]}),"instanceName":"1"});
            cPlane(context, id + "F26", {"entities" : qUnion([Q0]), "cplaneType" : CPlaneType.OFFSET, "offset" : 932.7 * mm, "oppositeDirection" : true, "width" : 150 * mm, "height" : 150 * mm});
        }
        {
            var Q0;
            Q0=qCreatedBy(id+"F26.planeOp",FACE);
            var sketch = newSketch(context, id + "F27", { "sketchPlane" : qUnion([Q0])});
            skLineSegment(sketch, "E107", {"start": v(-173.82, 56.15) * mm, "end": v(-173.82, 30) * mm, "construction": true});
            skLineSegment(sketch, "E108", {"start": v(-173.82, 30) * mm, "end": v(-199.07, 30) * mm, "construction": true});
            skLineSegment(sketch, "E109", {"start": v(-199.32, 42.15) * mm, "end": v(-199.32, 48.65) * mm});
            skLineSegment(sketch, "E110", {"start": v(-187.82, 56.15) * mm, "end": v(-173.82, 56.15) * mm});
            skPoint(sketch, "E111.visualSharp", {"position": v(-199.32, 56.15) * mm});
            skArc(sketch, "E111.filletArc", {"start": v(-191.82, 56.15) * mm, "mid": v(-197.13, 53.95) * mm, "end": v(-199.32, 48.65) * mm});
            skArc(sketch, "E112.0", {"start": v(-191.82, 53.25) * mm, "mid": v(-195.08, 51.9) * mm, "end": v(-196.42, 48.65) * mm});
            skLineSegment(sketch, "E113", {"start": v(-196.42, 48.65) * mm, "end": v(-196.42, 30) * mm});
            skLineSegment(sketch, "E114", {"start": v(-191.82, 53.25) * mm, "end": v(-173.82, 53.25) * mm});
            skLineSegment(sketch, "E115", {"start": v(-191.82, 56.15) * mm, "end": v(-190.82, 55.15) * mm});
            skLineSegment(sketch, "E116", {"start": v(-190.82, 55.15) * mm, "end": v(-189.82, 56.15) * mm});
            skLineSegment(sketch, "E117", {"start": v(-199.07, 30) * mm, "end": v(-199.07, 42.15) * mm});
            skLineSegment(sketch, "E118", {"start": v(-199.07, 42.15) * mm, "end": v(-199.32, 42.15) * mm});
            skLineSegment(sketch, "E119", {"start": v(-189.82, 56.15) * mm, "end": v(-188.82, 55.15) * mm});
            skLineSegment(sketch, "E120", {"start": v(-188.82, 55.15) * mm, "end": v(-187.82, 56.15) * mm});
            skLineSegment(sketch, "E121", {"start": v(-199.07, 30) * mm, "end": v(-199.77, 30) * mm, "construction": true});
            skLineSegment(sketch, "E122", {"start": v(-173.82, 56.15) * mm, "end": v(-173.82, 57.1) * mm, "construction": true});
            skLineSegment(sketch, "E123.MirrorCS", {"start": v(-157.82, 56.15) * mm, "end": v(-158.82, 55.15) * mm});
            skLineSegment(sketch, "E124.MirrorCS", {"start": v(-156.82, 55.15) * mm, "end": v(-157.82, 56.15) * mm});
            skLineSegment(sketch, "E125.MirrorCS", {"start": v(-158.82, 55.15) * mm, "end": v(-159.82, 56.15) * mm});
            skLineSegment(sketch, "E126.MirrorCS", {"start": v(-148.57, 42.15) * mm, "end": v(-148.32, 42.15) * mm});
            skLineSegment(sketch, "E127.MirrorCS", {"start": v(-155.82, 56.15) * mm, "end": v(-156.82, 55.15) * mm});
            skLineSegment(sketch, "E128.MirrorCS", {"start": v(-148.57, 30) * mm, "end": v(-147.87, 30) * mm, "construction": true});
            skLineSegment(sketch, "E129.MirrorCS", {"start": v(-148.32, 42.15) * mm, "end": v(-148.32, 48.65) * mm});
            skLineSegment(sketch, "E130.MirrorCS", {"start": v(-148.57, 30) * mm, "end": v(-148.57, 42.15) * mm});
            skArc(sketch, "E131.MirrorCS", {"start": v(-155.82, 53.25) * mm, "mid": v(-152.57, 51.9) * mm, "end": v(-151.22, 48.65) * mm});
            skLineSegment(sketch, "E132.MirrorCS", {"start": v(-151.22, 48.65) * mm, "end": v(-151.22, 30) * mm});
            skPoint(sketch, "E133.MirrorP", {"position": v(-148.32, 56.15) * mm});
            skArc(sketch, "E134.MirrorCS", {"start": v(-155.82, 56.15) * mm, "mid": v(-150.52, 53.95) * mm, "end": v(-148.32, 48.65) * mm});
            skLineSegment(sketch, "E135.MirrorCS", {"start": v(-159.82, 56.15) * mm, "end": v(-173.82, 56.15) * mm});
            skLineSegment(sketch, "E136.MirrorCS", {"start": v(-155.82, 53.25) * mm, "end": v(-173.82, 53.25) * mm});
            skLineSegment(sketch, "E137.MirrorCS", {"start": v(-148.57, 17.85) * mm, "end": v(-148.32, 17.85) * mm});
            skLineSegment(sketch, "E138.MirrorCS", {"start": v(-155.82, 3.85) * mm, "end": v(-156.82, 4.85) * mm});
            skLineSegment(sketch, "E139.MirrorCS", {"start": v(-157.82, 3.85) * mm, "end": v(-158.82, 4.85) * mm});
            skLineSegment(sketch, "E140.MirrorCS", {"start": v(-156.82, 4.85) * mm, "end": v(-157.82, 3.85) * mm});
            skLineSegment(sketch, "E141.MirrorCS", {"start": v(-158.82, 4.85) * mm, "end": v(-159.82, 3.85) * mm});
            skLineSegment(sketch, "E142.MirrorCS", {"start": v(-148.32, 17.85) * mm, "end": v(-148.32, 11.35) * mm});
            skLineSegment(sketch, "E143.MirrorCS", {"start": v(-155.82, 6.75) * mm, "end": v(-173.82, 6.75) * mm});
            skLineSegment(sketch, "E144.MirrorCS", {"start": v(-159.82, 3.85) * mm, "end": v(-173.82, 3.85) * mm});
            skArc(sketch, "E145.MirrorCS", {"start": v(-155.82, 3.85) * mm, "mid": v(-150.52, 6.05) * mm, "end": v(-148.32, 11.35) * mm});
            skLineSegment(sketch, "E146.MirrorCS", {"start": v(-151.22, 11.35) * mm, "end": v(-151.22, 30) * mm});
            skArc(sketch, "E147.MirrorCS", {"start": v(-155.82, 6.75) * mm, "mid": v(-152.57, 8.1) * mm, "end": v(-151.22, 11.35) * mm});
            skPoint(sketch, "E148.MirrorP", {"position": v(-148.32, 3.85) * mm});
            skLineSegment(sketch, "E149.MirrorCS", {"start": v(-148.57, 30) * mm, "end": v(-148.57, 17.85) * mm});
            skLineSegment(sketch, "E150.MirrorCS", {"start": v(-173.82, 3.85) * mm, "end": v(-173.82, 2.9) * mm, "construction": true});
            skLineSegment(sketch, "E151.MirrorCS", {"start": v(-188.82, 4.85) * mm, "end": v(-187.82, 3.85) * mm});
            skLineSegment(sketch, "E152.MirrorCS", {"start": v(-191.82, 3.85) * mm, "end": v(-190.82, 4.85) * mm});
            skLineSegment(sketch, "E153.MirrorCS", {"start": v(-199.07, 17.85) * mm, "end": v(-199.32, 17.85) * mm});
            skLineSegment(sketch, "E154.MirrorCS", {"start": v(-190.82, 4.85) * mm, "end": v(-189.82, 3.85) * mm});
            skLineSegment(sketch, "E155.MirrorCS", {"start": v(-189.82, 3.85) * mm, "end": v(-188.82, 4.85) * mm});
            skLineSegment(sketch, "E156.MirrorCS", {"start": v(-199.07, 30) * mm, "end": v(-199.07, 17.85) * mm});
            skLineSegment(sketch, "E157.MirrorCS", {"start": v(-199.32, 17.85) * mm, "end": v(-199.32, 11.35) * mm});
            skLineSegment(sketch, "E158.MirrorCS", {"start": v(-187.82, 3.85) * mm, "end": v(-173.82, 3.85) * mm});
            skPoint(sketch, "E159.MirrorP", {"position": v(-199.32, 3.85) * mm});
            skLineSegment(sketch, "E160.MirrorCS", {"start": v(-191.82, 6.75) * mm, "end": v(-173.82, 6.75) * mm});
            skArc(sketch, "E161.MirrorCS", {"start": v(-191.82, 3.85) * mm, "mid": v(-197.13, 6.05) * mm, "end": v(-199.32, 11.35) * mm});
            skLineSegment(sketch, "E162.MirrorCS", {"start": v(-196.42, 11.35) * mm, "end": v(-196.42, 30) * mm});
            skArc(sketch, "E163.MirrorCS", {"start": v(-191.82, 6.75) * mm, "mid": v(-195.08, 8.1) * mm, "end": v(-196.42, 11.35) * mm});
            skSolve(sketch);
        }
        {
            var Q0;
            Q0=qSketchRegion(id+"F27",true);
            var Q1;
            Q1 = qSketchRegion(id + "F27", true);
            extrude(context, id + "F28", {"entities" : qUnion([Q0, Q1]), "depth" : 462.5 * mm, "offsetDistance" : 25 * mm});
        }
        {
            var Q0;
            Q0=makeQuery(id+"F28.opExtrude","SWEPT_FACE",FACE,{"disambiguationData":[OSD([sQuery(id+"F27.wireOp",EDGE,"E144.MirrorCS"),sQuery(id+"F27.wireOp",EDGE,"E158.MirrorCS")])]});
            var sketch = newSketch(context, id + "F29", { "sketchPlane" : qUnion([Q0])});
            skLineSegment(sketch, "E164", {"start": v(173.82, 932.7) * mm, "end": v(173.82, 470.2) * mm, "construction": true});
            skLineSegment(sketch, "E165", {"start": v(173.82, 442.7) * mm, "end": v(173.82, 442.7) * mm});
            skCircle(sketch, "E166", {"center": v(173.82, 727.7) * mm, "radius": 6.25 * mm});
            skCircle(sketch, "E167", {"center": v(173.82, 627.7) * mm, "radius": 6.25 * mm});
            skCircle(sketch, "E168", {"center": v(173.82, 527.7) * mm, "radius": 6.25 * mm});
            skLineSegment(sketch, "E169", {"start": v(-34.52, 752.7) * mm, "end": v(403.84, 752.7) * mm, "construction": true});
            skSolve(sketch);
        }
        {
            var Q0;
            Q0 = qSketchRegion(id + "F29", true);
            var Q1;
            Q1=makeQuery(id+"F28.opExtrude","SWEPT_FACE",FACE,{"disambiguationData":[OSD([sQuery(id+"F27.wireOp",EDGE,"E110"),sQuery(id+"F27.wireOp",EDGE,"E135.MirrorCS")])]});
            extrude(context, id + "F30", {"entities" : qUnion([Q0]), "operationType" : NewBodyOperationType.REMOVE, "endBound" : BoundingType.UP_TO_SURFACE, "oppositeDirection" : true, "depth" : 25 * mm, "endBoundEntityFace" : qUnion([Q1]), "offsetDistance" : 25 * mm});
        }
        {
            var Q0;
            Q0=makeQuery(id+"F10.opExtrude","CAP_FACE",FACE,{"disambiguationData":[OSD([sQuery(id+"F9.wireOp",EDGE,"E40"),sQuery(id+"F9.wireOp",EDGE,"E41"),sQuery(id+"F9.wireOp",EDGE,"E42"),sQuery(id+"F9.wireOp",EDGE,"E43")])],"isStart":false});
            var sketch = newSketch(context, id + "F31", { "sketchPlane" : qUnion([Q0])});
            skCircle(sketch, "E170", {"center": v(173.82, 527.7) * mm, "radius": 6.25 * mm});
            skLineSegment(sketch, "E171", {"start": v(173.82, 650) * mm, "end": v(173.82, 171.1) * mm, "construction": true});
            skCircle(sketch, "E172", {"center": v(173.82, 627.7) * mm, "radius": 6.25 * mm});
            skSolve(sketch);
        }
        {
            var Q0;
            Q0 = qSketchRegion(id + "F31", true);
            var Q1;
            Q1=makeQuery(id+"F10.opExtrude","CAP_FACE",FACE,{"disambiguationData":[OSD([sQuery(id+"F9.wireOp",EDGE,"E40"),sQuery(id+"F9.wireOp",EDGE,"E41"),sQuery(id+"F9.wireOp",EDGE,"E42"),sQuery(id+"F9.wireOp",EDGE,"E43")])],"isStart":true});
            extrude(context, id + "F32", {"entities" : qUnion([Q0]), "operationType" : NewBodyOperationType.REMOVE, "endBound" : BoundingType.UP_TO_SURFACE, "oppositeDirection" : true, "depth" : 25 * mm, "endBoundEntityFace" : qUnion([Q1]), "offsetDistance" : 25 * mm});
        }
        {
            var Q0;
            Q0=makeQuery(id+"F28.opExtrude","SWEPT_FACE",FACE,{"disambiguationData":[OSD([sQuery(id+"F27.wireOp",EDGE,"E130.MirrorCS"),sQuery(id+"F27.wireOp",EDGE,"E149.MirrorCS")])]});
            var sketch = newSketch(context, id + "F33", { "sketchPlane" : qUnion([Q0])});
            skLineSegment(sketch, "E173", {"start": v(-30, 932.7) * mm, "end": v(-30, 646.19) * mm, "construction": true});
            skCircle(sketch, "E174", {"center": v(-30, 907.7) * mm, "radius": 6.25 * mm});
            skSolve(sketch);
        }
        {
            var Q0;
            Q0 = qSketchRegion(id + "F33", true);
            var Q1;
            Q1=makeQuery(id+"F28.opExtrude","SWEPT_FACE",FACE,{"disambiguationData":[OSD([sQuery(id+"F27.wireOp",EDGE,"E117"),sQuery(id+"F27.wireOp",EDGE,"E156.MirrorCS")])]});
            extrude(context, id + "F34", {"entities" : qUnion([Q0]), "operationType" : NewBodyOperationType.REMOVE, "endBound" : BoundingType.UP_TO_SURFACE, "oppositeDirection" : true, "depth" : 25 * mm, "endBoundEntityFace" : qUnion([Q1]), "offsetDistance" : 25 * mm});
        }
        {
            var Q0;
            Q0=makeQuery(id+"F28.opExtrude","SWEPT_FACE",FACE,{"disambiguationData":[OSD([sQuery(id+"F27.wireOp",EDGE,"E144.MirrorCS"),sQuery(id+"F27.wireOp",EDGE,"E158.MirrorCS")])]});
            cPlane(context, id + "F35", {"entities" : qUnion([Q0]), "cplaneType" : CPlaneType.OFFSET, "offset" : 300 * mm, "oppositeDirection" : true, "width" : 150 * mm, "height" : 150 * mm});
        }
        {
            var Q0;
            Q0=makeQuery(id+"F1.opExtrude","SWEPT_BODY",BODY,{"disambiguationData":[OSD([sQuery(id+"F0.wireOp",EDGE,"E0"),sQuery(id+"F0.wireOp",EDGE,"E1"),sQuery(id+"F0.wireOp",EDGE,"E2"),sQuery(id+"F0.wireOp",EDGE,"E3")])]});
            var Q1;
            Q1=makeQuery(id+"F10.opExtrude","SWEPT_BODY",BODY,{"disambiguationData":[OSD([sQuery(id+"F9.wireOp",EDGE,"E40"),sQuery(id+"F9.wireOp",EDGE,"E41"),sQuery(id+"F9.wireOp",EDGE,"E42"),sQuery(id+"F9.wireOp",EDGE,"E43")])]});
            var Q2;
            Q2=makeQuery(id+"F20.opExtrude","SWEPT_BODY",BODY,{"disambiguationData":[OSD([sQuery(id+"F19.wireOp",EDGE,"E83"),sQuery(id+"F19.wireOp",EDGE,"E84"),sQuery(id+"F19.wireOp",EDGE,"E85"),sQuery(id+"F19.wireOp",EDGE,"E86"),sQuery(id+"F19.wireOp",EDGE,"E87"),sQuery(id+"F19.wireOp",EDGE,"E88"),sQuery(id+"F19.wireOp",EDGE,"E89"),sQuery(id+"F19.wireOp",EDGE,"E90"),sQuery(id+"F19.wireOp",EDGE,"E94"),sQuery(id+"F19.wireOp",EDGE,"E95")])]});
            var Q3;
            Q3=makeQuery(id+"F25.opPattern","COPY",BODY,{"derivedFrom":makeQuery(id+"F20.opExtrude","SWEPT_BODY",BODY,{"disambiguationData":[OSD([sQuery(id+"F19.wireOp",EDGE,"E83"),sQuery(id+"F19.wireOp",EDGE,"E84"),sQuery(id+"F19.wireOp",EDGE,"E85"),sQuery(id+"F19.wireOp",EDGE,"E86"),sQuery(id+"F19.wireOp",EDGE,"E87"),sQuery(id+"F19.wireOp",EDGE,"E88"),sQuery(id+"F19.wireOp",EDGE,"E89"),sQuery(id+"F19.wireOp",EDGE,"E90"),sQuery(id+"F19.wireOp",EDGE,"E94"),sQuery(id+"F19.wireOp",EDGE,"E95")])]}),"instanceName":"1"});
            var Q4;
            Q4=makeQuery(id+"F18.opPattern","COPY",BODY,{"derivedFrom":makeQuery(id+"F1.opExtrude","SWEPT_BODY",BODY,{"disambiguationData":[OSD([sQuery(id+"F0.wireOp",EDGE,"E0"),sQuery(id+"F0.wireOp",EDGE,"E1"),sQuery(id+"F0.wireOp",EDGE,"E2"),sQuery(id+"F0.wireOp",EDGE,"E3")])]}),"instanceName":"1"});
            var Q5;
            Q5=makeQuery(id+"F28.opExtrude","SWEPT_BODY",BODY,{"disambiguationData":[OSD([sQuery(id+"F27.wireOp",EDGE,"E109"),sQuery(id+"F27.wireOp",EDGE,"E110"),sQuery(id+"F27.wireOp",EDGE,"E111.filletArc"),sQuery(id+"F27.wireOp",EDGE,"E112.0"),sQuery(id+"F27.wireOp",EDGE,"E113"),sQuery(id+"F27.wireOp",EDGE,"E114"),sQuery(id+"F27.wireOp",EDGE,"E115"),sQuery(id+"F27.wireOp",EDGE,"E116"),sQuery(id+"F27.wireOp",EDGE,"E117"),sQuery(id+"F27.wireOp",EDGE,"E118"),sQuery(id+"F27.wireOp",EDGE,"E119"),sQuery(id+"F27.wireOp",EDGE,"E120"),sQuery(id+"F27.wireOp",EDGE,"E123.MirrorCS"),sQuery(id+"F27.wireOp",EDGE,"E124.MirrorCS"),sQuery(id+"F27.wireOp",EDGE,"E125.MirrorCS"),sQuery(id+"F27.wireOp",EDGE,"E126.MirrorCS"),sQuery(id+"F27.wireOp",EDGE,"E127.MirrorCS"),sQuery(id+"F27.wireOp",EDGE,"E129.MirrorCS"),sQuery(id+"F27.wireOp",EDGE,"E130.MirrorCS"),sQuery(id+"F27.wireOp",EDGE,"E131.MirrorCS"),sQuery(id+"F27.wireOp",EDGE,"E132.MirrorCS"),sQuery(id+"F27.wireOp",EDGE,"E134.MirrorCS"),sQuery(id+"F27.wireOp",EDGE,"E135.MirrorCS"),sQuery(id+"F27.wireOp",EDGE,"E136.MirrorCS"),sQuery(id+"F27.wireOp",EDGE,"E137.MirrorCS"),sQuery(id+"F27.wireOp",EDGE,"E138.MirrorCS"),sQuery(id+"F27.wireOp",EDGE,"E139.MirrorCS"),sQuery(id+"F27.wireOp",EDGE,"E140.MirrorCS"),sQuery(id+"F27.wireOp",EDGE,"E141.MirrorCS"),sQuery(id+"F27.wireOp",EDGE,"E142.MirrorCS"),sQuery(id+"F27.wireOp",EDGE,"E143.MirrorCS"),sQuery(id+"F27.wireOp",EDGE,"E144.MirrorCS"),sQuery(id+"F27.wireOp",EDGE,"E145.MirrorCS"),sQuery(id+"F27.wireOp",EDGE,"E146.MirrorCS"),sQuery(id+"F27.wireOp",EDGE,"E147.MirrorCS"),sQuery(id+"F27.wireOp",EDGE,"E149.MirrorCS"),sQuery(id+"F27.wireOp",EDGE,"E151.MirrorCS"),sQuery(id+"F27.wireOp",EDGE,"E152.MirrorCS"),sQuery(id+"F27.wireOp",EDGE,"E153.MirrorCS"),sQuery(id+"F27.wireOp",EDGE,"E154.MirrorCS"),sQuery(id+"F27.wireOp",EDGE,"E155.MirrorCS"),sQuery(id+"F27.wireOp",EDGE,"E156.MirrorCS"),sQuery(id+"F27.wireOp",EDGE,"E157.MirrorCS"),sQuery(id+"F27.wireOp",EDGE,"E158.MirrorCS"),sQuery(id+"F27.wireOp",EDGE,"E160.MirrorCS"),sQuery(id+"F27.wireOp",EDGE,"E161.MirrorCS"),sQuery(id+"F27.wireOp",EDGE,"E162.MirrorCS"),sQuery(id+"F27.wireOp",EDGE,"E163.MirrorCS")])]});
            var Q6;
            Q6=qCreatedBy(id+"F35.planeOp",FACE);
            mirror(context, id + "F36", {"entities" : qUnion([Q0, Q1, Q2, Q3, Q4, Q5]), "mirrorPlane" : qUnion([Q6])});
        }
        {
            var Q0;
            Q0=qCreatedBy(id+"F35.planeOp",FACE);
            var sketch = newSketch(context, id + "F37", { "sketchPlane" : qUnion([Q0])});
            skPoint(sketch, "E175.MirrorP", {"position": v(-148.32, 921.22) * mm});
            skLineSegment(sketch, "E176", {"start": v(148.32, 946.7) * mm, "end": v(148.32, 940.2) * mm});
            skLineSegment(sketch, "E177", {"start": v(173.82, 932.7) * mm, "end": v(173.82, 958.85) * mm, "construction": true});
            skLineSegment(sketch, "E178", {"start": v(173.82, 958.85) * mm, "end": v(148.32, 958.85) * mm, "construction": true});
            skPoint(sketch, "E179.visualSharp", {"position": v(148.32, 932.7) * mm});
            skArc(sketch, "E179.filletArc", {"start": v(148.32, 940.2) * mm, "mid": v(150.52, 934.9) * mm, "end": v(155.82, 932.7) * mm});
            skLineSegment(sketch, "E180", {"start": v(148.57, 958.85) * mm, "end": v(148.57, 946.7) * mm});
            skLineSegment(sketch, "E181", {"start": v(148.57, 946.7) * mm, "end": v(148.32, 946.7) * mm});
            skArc(sketch, "E182.0", {"start": v(151.22, 940.2) * mm, "mid": v(152.57, 936.95) * mm, "end": v(155.82, 935.6) * mm});
            skLineSegment(sketch, "E183", {"start": v(151.22, 940.2) * mm, "end": v(151.22, 958.85) * mm});
            skLineSegment(sketch, "E184", {"start": v(155.82, 935.6) * mm, "end": v(173.82, 935.6) * mm});
            skLineSegment(sketch, "E185", {"start": v(159.82, 932.7) * mm, "end": v(173.82, 932.7) * mm});
            skLineSegment(sketch, "E186", {"start": v(155.82, 932.7) * mm, "end": v(156.82, 933.7) * mm});
            skLineSegment(sketch, "E187", {"start": v(156.82, 933.7) * mm, "end": v(157.82, 932.7) * mm});
            skLineSegment(sketch, "E188", {"start": v(157.82, 932.7) * mm, "end": v(158.82, 933.7) * mm});
            skLineSegment(sketch, "E189", {"start": v(158.82, 933.7) * mm, "end": v(159.82, 932.7) * mm});
            skLineSegment(sketch, "E190.MirrorCS", {"start": v(199.07, 946.7) * mm, "end": v(199.32, 946.7) * mm});
            skLineSegment(sketch, "E191.MirrorCS", {"start": v(190.82, 933.7) * mm, "end": v(189.82, 932.7) * mm});
            skLineSegment(sketch, "E192.MirrorCS", {"start": v(191.82, 932.7) * mm, "end": v(190.82, 933.7) * mm});
            skLineSegment(sketch, "E193.MirrorCS", {"start": v(189.82, 932.7) * mm, "end": v(188.82, 933.7) * mm});
            skLineSegment(sketch, "E194.MirrorCS", {"start": v(188.82, 933.7) * mm, "end": v(187.82, 932.7) * mm});
            skArc(sketch, "E195.MirrorCS", {"start": v(196.42, 940.2) * mm, "mid": v(195.08, 936.95) * mm, "end": v(191.82, 935.6) * mm});
            skArc(sketch, "E196.MirrorCS", {"start": v(199.32, 940.2) * mm, "mid": v(197.13, 934.9) * mm, "end": v(191.82, 932.7) * mm});
            skLineSegment(sketch, "E197.MirrorCS", {"start": v(199.07, 958.85) * mm, "end": v(199.07, 946.7) * mm});
            skLineSegment(sketch, "E198.MirrorCS", {"start": v(196.42, 940.2) * mm, "end": v(196.42, 958.85) * mm});
            skLineSegment(sketch, "E199.MirrorCS", {"start": v(191.82, 935.6) * mm, "end": v(173.82, 935.6) * mm});
            skLineSegment(sketch, "E200.MirrorCS", {"start": v(187.82, 932.7) * mm, "end": v(173.82, 932.7) * mm});
            skLineSegment(sketch, "E201.MirrorCS", {"start": v(199.32, 946.7) * mm, "end": v(199.32, 940.2) * mm});
            skPoint(sketch, "E202.MirrorP", {"position": v(199.32, 932.7) * mm});
            skLineSegment(sketch, "E203.MirrorCS", {"start": v(199.07, 971) * mm, "end": v(199.32, 971) * mm});
            skLineSegment(sketch, "E204.MirrorCS", {"start": v(190.82, 984) * mm, "end": v(189.82, 985) * mm});
            skLineSegment(sketch, "E205.MirrorCS", {"start": v(191.82, 985) * mm, "end": v(190.82, 984) * mm});
            skLineSegment(sketch, "E206.MirrorCS", {"start": v(189.82, 985) * mm, "end": v(188.82, 984) * mm});
            skLineSegment(sketch, "E207.MirrorCS", {"start": v(188.82, 984) * mm, "end": v(187.82, 985) * mm});
            skLineSegment(sketch, "E208.MirrorCS", {"start": v(199.07, 958.85) * mm, "end": v(199.07, 971) * mm});
            skArc(sketch, "E209.MirrorCS", {"start": v(199.32, 977.5) * mm, "mid": v(197.13, 982.8) * mm, "end": v(191.82, 985) * mm});
            skLineSegment(sketch, "E210.MirrorCS", {"start": v(191.82, 982.1) * mm, "end": v(173.82, 982.1) * mm});
            skPoint(sketch, "E211.MirrorP", {"position": v(199.32, 985) * mm});
            skLineSegment(sketch, "E212.MirrorCS", {"start": v(199.32, 971) * mm, "end": v(199.32, 977.5) * mm});
            skLineSegment(sketch, "E213.MirrorCS", {"start": v(196.42, 977.5) * mm, "end": v(196.42, 958.85) * mm});
            skArc(sketch, "E214.MirrorCS", {"start": v(196.42, 977.5) * mm, "mid": v(195.08, 980.75) * mm, "end": v(191.82, 982.1) * mm});
            skLineSegment(sketch, "E215.MirrorCS", {"start": v(187.82, 985) * mm, "end": v(173.82, 985) * mm});
            skLineSegment(sketch, "E216.MirrorCS", {"start": v(158.82, 984) * mm, "end": v(159.82, 985) * mm});
            skLineSegment(sketch, "E217.MirrorCS", {"start": v(156.82, 984) * mm, "end": v(157.82, 985) * mm});
            skLineSegment(sketch, "E218.MirrorCS", {"start": v(148.57, 971) * mm, "end": v(148.32, 971) * mm});
            skLineSegment(sketch, "E219.MirrorCS", {"start": v(155.82, 985) * mm, "end": v(156.82, 984) * mm});
            skLineSegment(sketch, "E220.MirrorCS", {"start": v(157.82, 985) * mm, "end": v(158.82, 984) * mm});
            skArc(sketch, "E221.MirrorCS", {"start": v(151.22, 977.5) * mm, "mid": v(152.57, 980.75) * mm, "end": v(155.82, 982.1) * mm});
            skLineSegment(sketch, "E222.MirrorCS", {"start": v(148.57, 958.85) * mm, "end": v(148.57, 971) * mm});
            skArc(sketch, "E223.MirrorCS", {"start": v(148.32, 977.5) * mm, "mid": v(150.52, 982.8) * mm, "end": v(155.82, 985) * mm});
            skLineSegment(sketch, "E224.MirrorCS", {"start": v(159.82, 985) * mm, "end": v(173.82, 985) * mm});
            skLineSegment(sketch, "E225.MirrorCS", {"start": v(151.22, 977.5) * mm, "end": v(151.22, 958.85) * mm});
            skLineSegment(sketch, "E226.MirrorCS", {"start": v(148.32, 971) * mm, "end": v(148.32, 977.5) * mm});
            skPoint(sketch, "E227.MirrorP", {"position": v(148.32, 985) * mm});
            skLineSegment(sketch, "E228.MirrorCS", {"start": v(155.82, 982.1) * mm, "end": v(173.82, 982.1) * mm});
            skSolve(sketch);
        }
        {
            var Q0;
            Q0 = qSketchRegion(id + "F37", true);
            var Q1;
            Q1=makeQuery(id+"F36.opPattern","COPY",FACE,{"derivedFrom":makeQuery(id+"F28.opExtrude","SWEPT_FACE",FACE,{"disambiguationData":[OSD([sQuery(id+"F27.wireOp",EDGE,"E144.MirrorCS"),sQuery(id+"F27.wireOp",EDGE,"E158.MirrorCS")])]}),"instanceName":"1"});
            var Q2;
            Q2=makeQuery(id+"F28.opExtrude","SWEPT_FACE",FACE,{"disambiguationData":[OSD([sQuery(id+"F27.wireOp",EDGE,"E144.MirrorCS"),sQuery(id+"F27.wireOp",EDGE,"E158.MirrorCS")])]});
            extrude(context, id + "F38", {"entities" : qUnion([Q0]), "endBound" : BoundingType.UP_TO_SURFACE, "oppositeDirection" : true, "depth" : 25 * mm, "endBoundEntityFace" : qUnion([Q1]), "offsetDistance" : 25 * mm, "hasSecondDirection" : true, "secondDirectionBound" : SecondDirectionBoundingType.UP_TO_SURFACE, "secondDirectionOppositeDirection" : false, "secondDirectionDepth" : 25 * mm, "secondDirectionBoundEntityFace" : qUnion([Q2])});
        }
        {
            var Q0;
            Q0=makeQuery(id+"F38.opExtrude","SWEPT_FACE",FACE,{"disambiguationData":[OSD([sQuery(id+"F37.wireOp",EDGE,"E180"),sQuery(id+"F37.wireOp",EDGE,"E222.MirrorCS")])]});
            var sketch = newSketch(context, id + "F39", { "sketchPlane" : qUnion([Q0])});
            skLineSegment(sketch, "E229", {"start": v(-3.85, 958.85) * mm, "end": v(-30, 958.85) * mm, "construction": true});
            skLineSegment(sketch, "E230", {"start": v(-30, 958.85) * mm, "end": v(-30, 1009.64) * mm, "construction": true});
            skLineSegment(sketch, "E231", {"start": v(-30, 958.85) * mm, "end": v(-56.15, 958.85) * mm, "construction": true});
            skCircle(sketch, "E232", {"center": v(-81.15, 958.85) * mm, "radius": 6.25 * mm});
            skCircle(sketch, "E233", {"center": v(-30, 958.85) * mm, "radius": 6.25 * mm});
            skCircle(sketch, "E234.MirrorC", {"center": v(-577.7, 958.85) * mm, "radius": 6.25 * mm});
            skCircle(sketch, "E235.MirrorC", {"center": v(-526.55, 958.85) * mm, "radius": 6.25 * mm});
            skLineSegment(sketch, "E236.MirrorCS", {"start": v(-577.7, 958.85) * mm, "end": v(-551.55, 958.85) * mm, "construction": true});
            skLineSegment(sketch, "E237.MirrorCS", {"start": v(-603.85, 958.85) * mm, "end": v(-577.7, 958.85) * mm, "construction": true});
            skLineSegment(sketch, "E238.MirrorCS", {"start": v(-577.7, 958.85) * mm, "end": v(-577.7, 1009.64) * mm, "construction": true});
            skSolve(sketch);
        }
        {
            var Q0;
            Q0 = qSketchRegion(id + "F39", true);
            var Q1;
            Q1=makeQuery(id+"F38.opExtrude","SWEPT_FACE",FACE,{"disambiguationData":[OSD([sQuery(id+"F37.wireOp",EDGE,"E197.MirrorCS"),sQuery(id+"F37.wireOp",EDGE,"E208.MirrorCS")])]});
            extrude(context, id + "F40", {"entities" : qUnion([Q0]), "operationType" : NewBodyOperationType.REMOVE, "endBound" : BoundingType.UP_TO_SURFACE, "oppositeDirection" : true, "depth" : 25 * mm, "endBoundEntityFace" : qUnion([Q1]), "offsetDistance" : 25 * mm});
        }
        {
            var Q0;
            Q0=makeQuery(id+"F38.opExtrude","SWEPT_FACE",FACE,{"disambiguationData":[OSD([sQuery(id+"F37.wireOp",EDGE,"E176")])]});
            var sketch = newSketch(context, id + "F41", { "sketchPlane" : qUnion([Q0])});
            skLineSegment(sketch, "E239", {"start": v(-106.15, 978.85) * mm, "end": v(-106.15, 938.85) * mm});
            skLineSegment(sketch, "E240", {"start": v(-106.15, 938.85) * mm, "end": v(-50, 882.7) * mm});
            skLineSegment(sketch, "E241", {"start": v(-50, 882.7) * mm, "end": v(-10, 882.7) * mm});
            skLineSegment(sketch, "E242", {"start": v(-10, 882.7) * mm, "end": v(-10, 978.85) * mm});
            skLineSegment(sketch, "E243", {"start": v(-10, 978.85) * mm, "end": v(-106.15, 978.85) * mm});
            skLineSegment(sketch, "E244", {"start": v(-106.15, 958.85) * mm, "end": v(-30, 958.85) * mm, "construction": true});
            skLineSegment(sketch, "E245", {"start": v(-30, 882.7) * mm, "end": v(-30, 958.85) * mm, "construction": true});
            skCircle(sketch, "E246", {"center": v(-30, 958.85) * mm, "radius": 6.25 * mm});
            skCircle(sketch, "E247", {"center": v(-81.15, 958.85) * mm, "radius": 6.25 * mm});
            skCircle(sketch, "E248", {"center": v(-30, 907.7) * mm, "radius": 6.25 * mm});
            skSolve(sketch);
        }
        {
            var Q0;
            Q0 = qSketchRegion(id + "F41", true);
            extrude(context, id + "F42", {"entities" : qUnion([Q0]), "depth" : 4 * mm, "offsetDistance" : 25 * mm});
        }
        {
            var Q0;
            Q0=makeQuery(id+"F42.opExtrude","SWEPT_EDGE",EDGE,{"disambiguationData":[OSD([sQuery(id+"F41.wireOp",EDGE,"E239"),sQuery(id+"F41.wireOp",EDGE,"E243")])]});
            var Q1;
            Q1=makeQuery(id+"F42.opExtrude","SWEPT_EDGE",EDGE,{"disambiguationData":[OSD([sQuery(id+"F41.wireOp",EDGE,"E239"),sQuery(id+"F41.wireOp",EDGE,"E240")])]});
            var Q2;
            Q2=makeQuery(id+"F42.opExtrude","SWEPT_EDGE",EDGE,{"disambiguationData":[OSD([sQuery(id+"F41.wireOp",EDGE,"E240"),sQuery(id+"F41.wireOp",EDGE,"E241")])]});
            var Q3;
            Q3=makeQuery(id+"F42.opExtrude","SWEPT_EDGE",EDGE,{"disambiguationData":[OSD([sQuery(id+"F41.wireOp",EDGE,"E241"),sQuery(id+"F41.wireOp",EDGE,"E242")])]});
            var Q4;
            Q4=makeQuery(id+"F42.opExtrude","SWEPT_EDGE",EDGE,{"disambiguationData":[OSD([sQuery(id+"F41.wireOp",EDGE,"E242"),sQuery(id+"F41.wireOp",EDGE,"E243")])]});
            fillet(context, id + "F43", {"entities" : qUnion([Q0, Q1, Q2, Q3, Q4]), "radius" : 7.5 * mm, "tangentPropagation" : true, "allowEdgeOverflow" : false});
        }
        {
            var Q0;
            Q0=makeQuery(id+"F42.opExtrude","SWEPT_BODY",BODY,{"disambiguationData":[OSD([sQuery(id+"F41.wireOp",EDGE,"E239"),sQuery(id+"F41.wireOp",EDGE,"E240"),sQuery(id+"F41.wireOp",EDGE,"E241"),sQuery(id+"F41.wireOp",EDGE,"E242"),sQuery(id+"F41.wireOp",EDGE,"E243"),sQuery(id+"F41.wireOp",EDGE,"E246"),sQuery(id+"F41.wireOp",EDGE,"E247"),sQuery(id+"F41.wireOp",EDGE,"E248")])]});
            var Q1;
            Q1=qCreatedBy(id+"F35.planeOp",FACE);
            mirror(context, id + "F44", {"entities" : qUnion([Q0]), "mirrorPlane" : qUnion([Q1])});
        }
        {
            var Q0;
            Q0=makeQuery(id+"F42.opExtrude","SWEPT_BODY",BODY,{"disambiguationData":[OSD([sQuery(id+"F41.wireOp",EDGE,"E239"),sQuery(id+"F41.wireOp",EDGE,"E240"),sQuery(id+"F41.wireOp",EDGE,"E241"),sQuery(id+"F41.wireOp",EDGE,"E242"),sQuery(id+"F41.wireOp",EDGE,"E243"),sQuery(id+"F41.wireOp",EDGE,"E246"),sQuery(id+"F41.wireOp",EDGE,"E247"),sQuery(id+"F41.wireOp",EDGE,"E248")])]});
            var Q1;
            Q1=makeQuery(id+"F44.opPattern","COPY",BODY,{"derivedFrom":makeQuery(id+"F42.opExtrude","SWEPT_BODY",BODY,{"disambiguationData":[OSD([sQuery(id+"F41.wireOp",EDGE,"E239"),sQuery(id+"F41.wireOp",EDGE,"E240"),sQuery(id+"F41.wireOp",EDGE,"E241"),sQuery(id+"F41.wireOp",EDGE,"E242"),sQuery(id+"F41.wireOp",EDGE,"E243"),sQuery(id+"F41.wireOp",EDGE,"E246"),sQuery(id+"F41.wireOp",EDGE,"E247"),sQuery(id+"F41.wireOp",EDGE,"E248")])]}),"instanceName":"1"});
            var Q2;
            Q2=qCreatedBy(id+"F17.planeOp",FACE);
            mirror(context, id + "F45", {"entities" : qUnion([Q0, Q1]), "mirrorPlane" : qUnion([Q2])});
        }
        {
            var Q0;
            {var subQ0=sQuery(id+"F0.wireOp",EDGE,"E0");Q0=makeQuery(id+"F4.boolean.opBoolean","SPLIT",FACE,{"disambiguationData":[TD([makeQuery(id+"F4.opExtrude","SWEPT_FACE",FACE,{"disambiguationData":[OSD([sQuery(id+"F3.wireOp",EDGE,"E8")])]})])],"derivedFrom":makeQuery(id+"F1.opExtrude","SWEPT_FACE",FACE,{"disambiguationData":[OSD([subQ0])]})});}
            var sketch = newSketch(context, id + "F46", { "sketchPlane" : qUnion([Q0])});
            skLineSegment(sketch, "E249", {"start": v(-607.7, 170.12) * mm, "end": v(-607.7, 130.12) * mm});
            skLineSegment(sketch, "E250", {"start": v(-607.7, 130.12) * mm, "end": v(0, 130.12) * mm});
            skLineSegment(sketch, "E251", {"start": v(0, 130.12) * mm, "end": v(0, 170.12) * mm});
            skLineSegment(sketch, "E252", {"start": v(0, 170.12) * mm, "end": v(-607.7, 170.12) * mm});
            skLineSegment(sketch, "E253", {"start": v(-607.7, 150.12) * mm, "end": v(0, 150.12) * mm, "construction": true});
            skCircle(sketch, "E254", {"center": v(-577.7, 150.12) * mm, "radius": 6.25 * mm});
            skCircle(sketch, "E255.MirrorC", {"center": v(-30, 150.12) * mm, "radius": 6.25 * mm});
            skSolve(sketch);
        }
        {
            var Q0;
            Q0 = qSketchRegion(id + "F46", true);
            extrude(context, id + "F47", {"entities" : qUnion([Q0]), "depth" : 4 * mm, "offsetDistance" : 25 * mm});
        }
        {
            var Q0;
            Q0=makeQuery(id+"F38.opExtrude","SWEPT_FACE",FACE,{"disambiguationData":[OSD([sQuery(id+"F37.wireOp",EDGE,"E215.MirrorCS"),sQuery(id+"F37.wireOp",EDGE,"E224.MirrorCS")])]});
            var sketch = newSketch(context, id + "F48", { "sketchPlane" : qUnion([Q0])});
            skLineSegment(sketch, "E256", {"start": v(-173.82, -603.85) * mm, "end": v(-173.82, -3.85) * mm, "construction": true});
            skCircle(sketch, "E257", {"center": v(-173.82, -103.85) * mm, "radius": 6.25 * mm});
            skCircle(sketch, "E258.MirrorC", {"center": v(-173.82, -503.85) * mm, "radius": 6.25 * mm});
            skCircle(sketch, "E259", {"center": v(-173.82, -303.85) * mm, "radius": 6.25 * mm});
            skSolve(sketch);
        }
        {
            var Q0;
            Q0 = qSketchRegion(id + "F48", true);
            var Q1;
            Q1=makeQuery(id+"F38.opExtrude","SWEPT_FACE",FACE,{"disambiguationData":[OSD([sQuery(id+"F37.wireOp",EDGE,"E185"),sQuery(id+"F37.wireOp",EDGE,"E200.MirrorCS")])]});
            extrude(context, id + "F49", {"entities" : qUnion([Q0]), "operationType" : NewBodyOperationType.REMOVE, "endBound" : BoundingType.UP_TO_SURFACE, "oppositeDirection" : true, "depth" : 25 * mm, "endBoundEntityFace" : qUnion([Q1]), "offsetDistance" : 25 * mm});
        }
        {
            var Q0;
            Q0=makeQuery(id+"F47.opExtrude","SWEPT_EDGE",EDGE,{"disambiguationData":[OSD([sQuery(id+"F46.wireOp",EDGE,"E249"),sQuery(id+"F46.wireOp",EDGE,"E252")])]});
            var Q1;
            Q1=makeQuery(id+"F47.opExtrude","SWEPT_EDGE",EDGE,{"disambiguationData":[OSD([sQuery(id+"F46.wireOp",EDGE,"E249"),sQuery(id+"F46.wireOp",EDGE,"E250")])]});
            var Q2;
            Q2=makeQuery(id+"F47.opExtrude","SWEPT_EDGE",EDGE,{"disambiguationData":[OSD([sQuery(id+"F46.wireOp",EDGE,"E250"),sQuery(id+"F46.wireOp",EDGE,"E251")])]});
            var Q3;
            Q3=makeQuery(id+"F47.opExtrude","SWEPT_EDGE",EDGE,{"disambiguationData":[OSD([sQuery(id+"F46.wireOp",EDGE,"E251"),sQuery(id+"F46.wireOp",EDGE,"E252")])]});
            fillet(context, id + "F50", {"entities" : qUnion([Q0, Q1, Q2, Q3]), "radius" : 10 * mm, "tangentPropagation" : true, "allowEdgeOverflow" : false});
        }
        {
            var Q0;
            Q0=makeQuery(id+"F47.opExtrude","SWEPT_BODY",BODY,{"disambiguationData":[OSD([sQuery(id+"F46.wireOp",EDGE,"E249"),sQuery(id+"F46.wireOp",EDGE,"E250"),sQuery(id+"F46.wireOp",EDGE,"E251"),sQuery(id+"F46.wireOp",EDGE,"E252"),sQuery(id+"F46.wireOp",EDGE,"E254"),sQuery(id+"F46.wireOp",EDGE,"E255.MirrorC")])]});
            var Q1;
            Q1=qCreatedBy(id+"F17.planeOp",FACE);
            mirror(context, id + "F51", {"entities" : qUnion([Q0]), "mirrorPlane" : qUnion([Q1])});
        }
        {
            var Q0;
            Q0=qCreatedBy(id+"F17.planeOp",FACE);
            var sketch = newSketch(context, id + "F52", { "sketchPlane" : qUnion([Q0])});
            skLineSegment(sketch, "E260", {"start": v(573.85, 1055) * mm, "end": v(573.85, 985) * mm});
            skLineSegment(sketch, "E261", {"start": v(573.85, 985) * mm, "end": v(33.85, 985) * mm});
            skLineSegment(sketch, "E262", {"start": v(33.85, 985) * mm, "end": v(33.85, 1055) * mm});
            skLineSegment(sketch, "E263", {"start": v(33.85, 1055) * mm, "end": v(37.85, 1055) * mm});
            skLineSegment(sketch, "E264", {"start": v(37.85, 1055) * mm, "end": v(37.85, 989) * mm});
            skLineSegment(sketch, "E265", {"start": v(37.85, 989) * mm, "end": v(569.85, 989) * mm});
            skLineSegment(sketch, "E266", {"start": v(569.85, 989) * mm, "end": v(569.85, 1055) * mm});
            skLineSegment(sketch, "E267", {"start": v(569.85, 1055) * mm, "end": v(573.85, 1055) * mm});
            skLineSegment(sketch, "E268", {"start": v(573.85, 1035) * mm, "end": v(569.85, 1035) * mm, "construction": true});
            skLineSegment(sketch, "E269", {"start": v(37.85, 1035) * mm, "end": v(33.85, 1035) * mm, "construction": true});
            skSolve(sketch);
        }
        {
            var Q0;
            Q0 = qSketchRegion(id + "F52", true);
            extrude(context, id + "F53", {"entities" : qUnion([Q0]), "endBound" : BoundingType.SYMMETRIC, "depth" : 40 * mm, "offsetDistance" : 25 * mm});
        }
        {
            var Q0;
            Q0=makeQuery(id+"F53.opExtrude","SWEPT_FACE",FACE,{"disambiguationData":[OSD([sQuery(id+"F52.wireOp",EDGE,"E265")])]});
            var sketch = newSketch(context, id + "F54", { "sketchPlane" : qUnion([Q0])});
            skCircle(sketch, "E270", {"center": v(-173.82, -103.85) * mm, "radius": 6.25 * mm});
            skCircle(sketch, "E271", {"center": v(-173.82, -503.85) * mm, "radius": 6.25 * mm});
            skCircle(sketch, "E272", {"center": v(-173.82, -303.85) * mm, "radius": 6.25 * mm});
            skSolve(sketch);
        }
        {
            var Q0;
            Q0 = qSketchRegion(id + "F54", true);
            var Q1;
            Q1=makeQuery(id+"F53.opExtrude","SWEPT_FACE",FACE,{"disambiguationData":[OSD([sQuery(id+"F52.wireOp",EDGE,"E261")])]});
            extrude(context, id + "F55", {"entities" : qUnion([Q0]), "operationType" : NewBodyOperationType.REMOVE, "endBound" : BoundingType.UP_TO_SURFACE, "oppositeDirection" : true, "depth" : 25 * mm, "endBoundEntityFace" : qUnion([Q1]), "offsetDistance" : 25 * mm});
        }
        {
            var Q0;
            Q0=makeQuery(id+"F53.opExtrude","CAP_EDGE",EDGE,{"disambiguationData":[OSD([sQuery(id+"F52.wireOp",EDGE,"E263")])],"isStart":true});
            var Q1;
            Q1=makeQuery(id+"F53.opExtrude","CAP_EDGE",EDGE,{"disambiguationData":[OSD([sQuery(id+"F52.wireOp",EDGE,"E263")])],"isStart":false});
            var Q2;
            Q2=makeQuery(id+"F53.opExtrude","CAP_EDGE",EDGE,{"disambiguationData":[OSD([sQuery(id+"F52.wireOp",EDGE,"E267")])],"isStart":false});
            var Q3;
            Q3=makeQuery(id+"F53.opExtrude","CAP_EDGE",EDGE,{"disambiguationData":[OSD([sQuery(id+"F52.wireOp",EDGE,"E267")])],"isStart":true});
            fillet(context, id + "F56", {"entities" : qUnion([Q0, Q1, Q2, Q3]), "radius" : 20 * mm, "tangentPropagation" : true, "allowEdgeOverflow" : false});
        }
        {
            var Q0;
            Q0=qCreatedBy(id+"F35.planeOp",FACE);
            var sketch = newSketch(context, id + "F57", { "sketchPlane" : qUnion([Q0])});
            skCircle(sketch, "E273", {"center": v(173.82, 1035) * mm, "radius": 6.25 * mm});
            skSolve(sketch);
        }
        {
            var Q0;
            Q0 = qSketchRegion(id + "F57", true);
            var Q1;
            Q1=makeQuery(id+"F53.opExtrude","SWEPT_FACE",FACE,{"disambiguationData":[OSD([sQuery(id+"F52.wireOp",EDGE,"E260")])]});
            var Q2;
            Q2=makeQuery(id+"F53.opExtrude","SWEPT_FACE",FACE,{"disambiguationData":[OSD([sQuery(id+"F52.wireOp",EDGE,"E262")])]});
            extrude(context, id + "F58", {"entities" : qUnion([Q0]), "operationType" : NewBodyOperationType.REMOVE, "endBound" : BoundingType.UP_TO_SURFACE, "oppositeDirection" : true, "depth" : 25 * mm, "endBoundEntityFace" : qUnion([Q1]), "offsetDistance" : 25 * mm, "hasSecondDirection" : true, "secondDirectionBound" : SecondDirectionBoundingType.UP_TO_SURFACE, "secondDirectionOppositeDirection" : false, "secondDirectionDepth" : 25 * mm, "secondDirectionBoundEntityFace" : qUnion([Q2])});
        }
        {
            var Q0;
            Q0=qCreatedBy(id+"F35.planeOp",FACE);
            var sketch = newSketch(context, id + "F59", { "sketchPlane" : qUnion([Q0])});
            skCircle(sketch, "E274", {"center": v(173.82, 1035) * mm, "radius": 5.9 * mm});
            skSolve(sketch);
        }
        {
            var Q0;
            Q0 = qSketchRegion(id + "F59", true);
            extrude(context, id + "F60", {"entities" : qUnion([Q0]), "endBound" : BoundingType.SYMMETRIC, "depth" : 580 * mm, "offsetDistance" : 25 * mm});
        }
        {
            var Q0;
            Q0=makeQuery(id+"F60.opExtrude","CAP_EDGE",EDGE,{"disambiguationData":[OSD([sQuery(id+"F59.wireOp",EDGE,"E274")])],"isStart":false});
            var Q1;
            Q1=makeQuery(id+"F60.opExtrude","CAP_EDGE",EDGE,{"disambiguationData":[OSD([sQuery(id+"F59.wireOp",EDGE,"E274")])],"isStart":true});
            chamfer(context, id + "F61", {"entities" : qUnion([Q0, Q1]), "width" : 2 * mm, "tangentPropagation" : true});
        }
        {
            var Q0;
            Q0=qCreatedBy(id+"F35.planeOp",FACE);
            var sketch = newSketch(context, id + "F62", { "sketchPlane" : qUnion([Q0])});
            skCircle(sketch, "E275", {"center": v(173.82, 1035) * mm, "radius": 30 * mm});
            skCircle(sketch, "E276", {"center": v(173.82, 1035) * mm, "radius": 6.5 * mm});
            skSolve(sketch);
        }
        {
            var Q0;
            Q0 = qSketchRegion(id + "F62", true);
            extrude(context, id + "F63", {"entities" : qUnion([Q0]), "endBound" : BoundingType.SYMMETRIC, "depth" : 520 * mm, "offsetDistance" : 25 * mm});
        }
        {
            var Q0;
            Q0=makeQuery(id+"F63.opExtrude","CAP_EDGE",EDGE,{"disambiguationData":[OSD([sQuery(id+"F62.wireOp",EDGE,"E275")])],"isStart":false});
            var Q1;
            Q1=makeQuery(id+"F63.opExtrude","CAP_EDGE",EDGE,{"disambiguationData":[OSD([sQuery(id+"F62.wireOp",EDGE,"E275")])],"isStart":true});
            chamfer(context, id + "F64", {"entities" : qUnion([Q0, Q1]), "width" : 7.5 * mm, "tangentPropagation" : true});
        }
        {
            var Q0;
            Q0=makeQuery(id+"F63.opExtrude","SWEPT_FACE",FACE,{"disambiguationData":[OSD([sQuery(id+"F62.wireOp",EDGE,"E275")])]});
            cPlane(context, id + "F65", {"entities" : qUnion([Q0]), "cplaneType" : CPlaneType.LINE_ANGLE, "offset" : 25 * mm, "angle" : 0 * degree, "width" : 150 * mm, "height" : 150 * mm});
        }
    });
